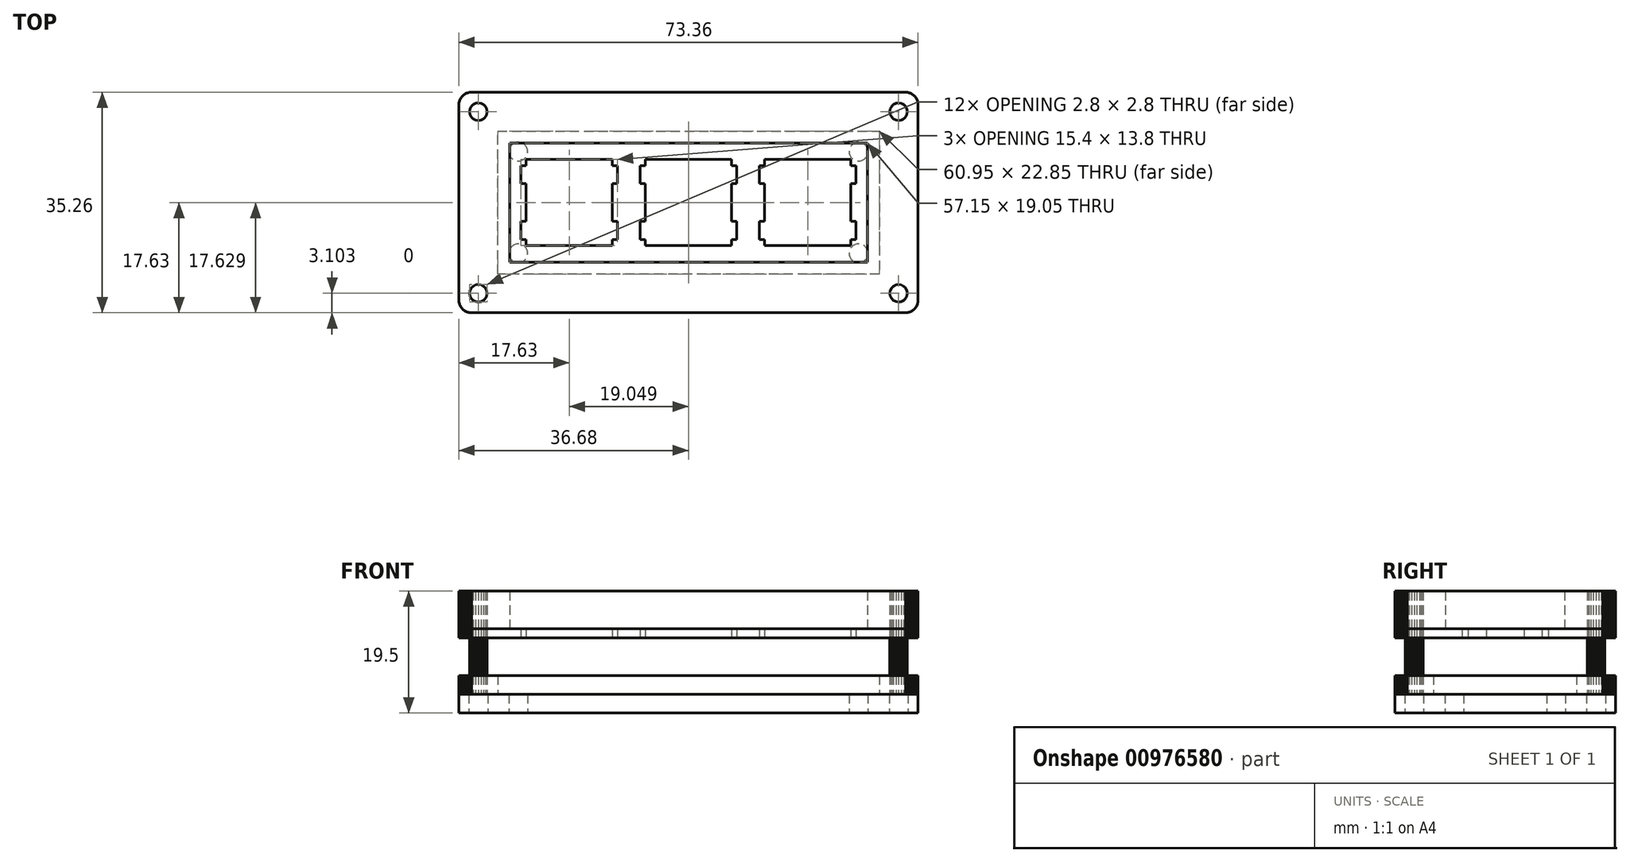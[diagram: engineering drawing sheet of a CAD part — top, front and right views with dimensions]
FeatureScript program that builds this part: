
annotation { "Feature Type Name" : "Feature", "Feature Type Description" : "" }
export const myFeature = defineFeature(function(context is Context, id is Id, definition is map)
    precondition{}
    {
        {
            assignVariable(context, id + "F0", {"name" : "Thickness", "anyValue" : 3});
        }
        {
            var Q0;
            Q0=qCreatedBy(makeId("Top.planeOp"),FACE);
            var sketch = newSketch(context, id + "F1", { "sketchPlane" : qUnion([Q0])});
            skLineSegment(sketch, "E0", {"start": v(36.68, 15.63) * mm, "end": v(36.68, -15.63) * mm});
            skLineSegment(sketch, "E1", {"start": v(34.68, -17.63) * mm, "end": v(-34.68, -17.63) * mm});
            skLineSegment(sketch, "E2", {"start": v(-36.68, -15.63) * mm, "end": v(-36.68, 15.63) * mm});
            skLineSegment(sketch, "E3", {"start": v(-34.68, 17.63) * mm, "end": v(34.68, 17.63) * mm});
            skCircle(sketch, "E4", {"center": v(-27.18, 8.13) * mm, "radius": 1.5 * mm});
            skCircle(sketch, "E5", {"center": v(-27.18, 8.13) * mm, "radius": 9.5 * mm, "construction": true});
            skPoint(sketch, "E6.visualSharp", {"position": v(-36.68, -17.63) * mm});
            skArc(sketch, "E6.filletArc", {"start": v(-36.68, -15.63) * mm, "mid": v(-36.09, -17.04) * mm, "end": v(-34.68, -17.63) * mm});
            skPoint(sketch, "E7.visualSharp", {"position": v(36.68, -17.63) * mm});
            skArc(sketch, "E7.filletArc", {"start": v(34.68, -17.63) * mm, "mid": v(36.09, -17.04) * mm, "end": v(36.68, -15.63) * mm});
            skPoint(sketch, "E8.visualSharp", {"position": v(36.68, 17.63) * mm});
            skArc(sketch, "E8.filletArc", {"start": v(36.68, 15.63) * mm, "mid": v(36.09, 17.04) * mm, "end": v(34.68, 17.63) * mm});
            skPoint(sketch, "E9.visualSharp", {"position": v(-36.68, 17.63) * mm});
            skArc(sketch, "E9.filletArc", {"start": v(-34.68, 17.63) * mm, "mid": v(-36.09, 17.04) * mm, "end": v(-36.68, 15.63) * mm});
            skCircle(sketch, "E10", {"center": v(33.58, 14.53) * mm, "radius": 3.1 * mm, "construction": true});
            skCircle(sketch, "E11", {"center": v(33.58, 14.53) * mm, "radius": 1.5 * mm});
            skCircle(sketch, "E12.MirrorC", {"center": v(33.58, -14.53) * mm, "radius": 1.5 * mm});
            skCircle(sketch, "E13.MirrorC", {"center": v(-33.58, 14.53) * mm, "radius": 1.5 * mm});
            skCircle(sketch, "E14.MirrorC", {"center": v(-33.58, -14.53) * mm, "radius": 1.5 * mm});
            skCircle(sketch, "E15.MirrorC", {"center": v(27.18, 8.13) * mm, "radius": 1.5 * mm});
            skCircle(sketch, "E16.MirrorC", {"center": v(-27.18, -8.13) * mm, "radius": 1.5 * mm});
            skCircle(sketch, "E17.MirrorC", {"center": v(27.18, -8.13) * mm, "radius": 1.5 * mm});
            skSolve(sketch);
        }
        {
            var Q0;
            Q0 = qSketchRegion(id + "F1", true);
            extrude(context, id + "F2", {"entities" : qUnion([Q0]), "depth" : (getVariable(context, 'Thickness')) * mm, "offsetDistance" : 25 * mm});
        }
        {
            var Q0;
            Q0=makeQuery(id+"F2.opExtrude","CAP_FACE",FACE,{"disambiguationData":[OSD([sQuery(id+"F1.wireOp",EDGE,"f38d5113-8ffd-432d-a3ce-a915938ce8ef"),sQuery(id+"F1.wireOp",EDGE,"30d00d2a-8399-40ac-ba43-e3ae4fa62f4f"),sQuery(id+"F1.wireOp",EDGE,"33de4b6a-8df2-4582-920f-f16a76d6a48d"),sQuery(id+"F1.wireOp",EDGE,"dd7a822c-130c-4706-b44d-d1e14abfd110"),sQuery(id+"F1.wireOp",EDGE,"c533de15-2e03-4a6f-b7a6-2e9cb061479b"),sQuery(id+"F1.wireOp",EDGE,"1dfa1c6c-949b-4392-be26-7293bec304e9"),sQuery(id+"F1.wireOp",EDGE,"79b63b09-4684-42a3-82d4-33271dc96dd7"),sQuery(id+"F1.wireOp",EDGE,"c6cd64e9-58d5-430f-8fd8-64eae907adb3"),sQuery(id+"F1.wireOp",EDGE,"a9528a18-83ce-47e4-8030-754601af9eb3"),sQuery(id+"F1.wireOp",EDGE,"cd46a195-92e7-4e63-b4f0-881a531f52bb"),sQuery(id+"F1.wireOp",EDGE,"56d33d33-9960-4a7a-86af-0e57c873a139"),sQuery(id+"F1.wireOp",EDGE,"8febe79d-c26d-47ca-a997-6ddbf6247f7f"),sQuery(id+"F1.wireOp",EDGE,"1b81442f-1442-4f9c-ac81-b0700e3801b3"),sQuery(id+"F1.wireOp",EDGE,"bce25026-a245-4289-a49b-b4b12a412b04"),sQuery(id+"F1.wireOp",EDGE,"256a1b4b-6397-493c-808c-40f05bf4c5e3"),sQuery(id+"F1.wireOp",EDGE,"982427ee-fb93-4e7f-9e5f-c007e6e26276"),sQuery(id+"F1.wireOp",EDGE,"e8128256-5901-4357-a0be-eaef1402cac8"),sQuery(id+"F1.wireOp",EDGE,"ce55bd8c-7602-4f65-abef-ba81b887f1be"),sQuery(id+"F1.wireOp",EDGE,"389a8022-4a1a-4ebd-a71b-27301e9d4ff6"),sQuery(id+"F1.wireOp",EDGE,"ce64c4c0-22d1-436f-a547-7537afd4866e"),sQuery(id+"F1.wireOp",EDGE,"E0"),sQuery(id+"F1.wireOp",EDGE,"e7bae28c-2ccc-4f20-96f0-a530882d5159"),sQuery(id+"F1.wireOp",EDGE,"1336ac6d-c182-419d-8f47-5aac0d18e762"),sQuery(id+"F1.wireOp",EDGE,"b2a7ba0f-895a-4bb6-a783-6d883c045cbe"),sQuery(id+"F1.wireOp",EDGE,"51b79f1e-a1b5-4bf4-937f-2afb163cf299"),sQuery(id+"F1.wireOp",EDGE,"549b87ac-e324-453b-b570-1453983d1911"),sQuery(id+"F1.wireOp",EDGE,"4242826b-0d45-4b2e-b694-fd388aa842fb"),sQuery(id+"F1.wireOp",EDGE,"c10ba44a-b5aa-45ae-bf6a-75690cab2dd6"),sQuery(id+"F1.wireOp",EDGE,"8177ea96-e12c-463d-a123-4af6399735c3"),sQuery(id+"F1.wireOp",EDGE,"58842294-a54e-47b9-86a7-91804475791d"),sQuery(id+"F1.wireOp",EDGE,"1daaa4ac-2799-49ed-8cf0-012224148010"),sQuery(id+"F1.wireOp",EDGE,"a375905a-4df6-48c9-a9bc-60ca1bae9196"),sQuery(id+"F1.wireOp",EDGE,"df5412a8-c126-4beb-a6d7-e5caac17dc0e"),sQuery(id+"F1.wireOp",EDGE,"0a7991f6-c764-42fb-b197-93e5d7973440"),sQuery(id+"F1.wireOp",EDGE,"db6fbf27-b7a6-43e2-ad22-b1f5cb7f6f55"),sQuery(id+"F1.wireOp",EDGE,"c78e91c3-a6b3-40c6-9ba2-7427c3ae4570"),sQuery(id+"F1.wireOp",EDGE,"1da2b595-4f5a-4a08-b72b-7e329805d670"),sQuery(id+"F1.wireOp",EDGE,"b998bcce-a593-4696-85a6-c582ec4e01af"),sQuery(id+"F1.wireOp",EDGE,"3c900711-9d2c-45f7-b880-0ee555895d99"),sQuery(id+"F1.wireOp",EDGE,"a664491b-32bc-47fb-82bc-0ab575ecea55"),sQuery(id+"F1.wireOp",EDGE,"0b5283cb-b386-4d68-bacd-65cfa7a1c687"),sQuery(id+"F1.wireOp",EDGE,"E1"),sQuery(id+"F1.wireOp",EDGE,"dc151aaf-655b-4e22-9e08-b51a414cdedc"),sQuery(id+"F1.wireOp",EDGE,"49712529-a297-4864-9951-9f888228fd79"),sQuery(id+"F1.wireOp",EDGE,"e018c4f9-948b-427d-ab6c-159fd14e4654"),sQuery(id+"F1.wireOp",EDGE,"b4c8d362-4280-49e8-b707-11ba0145ad9e"),sQuery(id+"F1.wireOp",EDGE,"e4ff2872-b3dd-4565-8f3a-b1d815be933f"),sQuery(id+"F1.wireOp",EDGE,"4f95d7c4-3227-4e30-a015-5dc2aef1d5b8"),sQuery(id+"F1.wireOp",EDGE,"7d5e0655-794f-4f1c-811a-7c8bca8cb441"),sQuery(id+"F1.wireOp",EDGE,"06cd70f3-8a57-4482-8df6-4ae0e3f2c176"),sQuery(id+"F1.wireOp",EDGE,"79ffc42a-8afc-40c3-b99c-81495eff8d88"),sQuery(id+"F1.wireOp",EDGE,"42f66c54-dfdb-4538-af7b-f42205d213f2"),sQuery(id+"F1.wireOp",EDGE,"4107d0d6-0b50-4649-80d2-5ef7e23b521e"),sQuery(id+"F1.wireOp",EDGE,"40e89e02-920e-4762-a084-e2b73f78281e"),sQuery(id+"F1.wireOp",EDGE,"fe9b1155-c610-44b2-a0b0-31eb3f0e455a"),sQuery(id+"F1.wireOp",EDGE,"73f3c45d-f342-4798-9e75-ac507e4c3c51"),sQuery(id+"F1.wireOp",EDGE,"094ff1a6-3b8b-4ac9-81fa-9bd9003943b7"),sQuery(id+"F1.wireOp",EDGE,"f8d24ccc-6bb8-41f9-afa7-affc31c8a13a"),sQuery(id+"F1.wireOp",EDGE,"f2db9464-d5ad-4da8-bc6d-19101f4076d9"),sQuery(id+"F1.wireOp",EDGE,"defc6b11-d794-425b-b4a3-06b1fb4b3a05"),sQuery(id+"F1.wireOp",EDGE,"abc8f65d-411d-4283-8a50-7cb67d340370"),sQuery(id+"F1.wireOp",EDGE,"cac6a9b9-9d93-4d5c-ad04-d05eb65cdc37"),sQuery(id+"F1.wireOp",EDGE,"E2"),sQuery(id+"F1.wireOp",EDGE,"1b493a45-cd4b-48a1-8403-62bc6a5772fd"),sQuery(id+"F1.wireOp",EDGE,"3576eeaf-6626-4881-aa94-039e0b64bb02"),sQuery(id+"F1.wireOp",EDGE,"5d0b7610-6fbf-4a3c-89f8-b3cf9798b51e"),sQuery(id+"F1.wireOp",EDGE,"ef7b6dab-872b-43b9-8f18-2a554d21f1c5"),sQuery(id+"F1.wireOp",EDGE,"702b8a5a-b0f8-4392-bb79-e2564fd4a175"),sQuery(id+"F1.wireOp",EDGE,"fb67655c-e3e3-4c0d-af6e-f14e7b25c453"),sQuery(id+"F1.wireOp",EDGE,"84ab0164-69e0-4c3c-a998-7971c5eca7ff"),sQuery(id+"F1.wireOp",EDGE,"f57c4b1b-64ee-44b1-9523-b8aed98779c7"),sQuery(id+"F1.wireOp",EDGE,"c5eadbd6-3ef8-4954-b175-27f3b5fe7724"),sQuery(id+"F1.wireOp",EDGE,"9ed46d83-222e-4792-a6c7-6fce6fe02704"),sQuery(id+"F1.wireOp",EDGE,"89c49cfb-4cd2-4b6f-8936-88e12b2d1e60"),sQuery(id+"F1.wireOp",EDGE,"4376ecf0-2db7-4b48-bea3-0de71fc5ea1c"),sQuery(id+"F1.wireOp",EDGE,"75b1cf93-37d0-4452-91ae-a9c5d2c97683"),sQuery(id+"F1.wireOp",EDGE,"3614327f-aa34-4ffd-8e4f-bcaeb5bf0a6c"),sQuery(id+"F1.wireOp",EDGE,"779057a4-3d89-47b9-81ca-a53b9e90171e"),sQuery(id+"F1.wireOp",EDGE,"6ee2b408-d537-4a72-87c2-fd9683a19ca6"),sQuery(id+"F1.wireOp",EDGE,"23edfa7d-6738-4f5a-81be-73427f6a28ee"),sQuery(id+"F1.wireOp",EDGE,"e48bd3fa-4649-480f-9b1a-c6254d94e219"),sQuery(id+"F1.wireOp",EDGE,"12005d63-deb8-4797-ae3c-77c9ec96a49e"),sQuery(id+"F1.wireOp",EDGE,"5feb5ef9-fb39-4188-8368-4f7ee21595f9"),sQuery(id+"F1.wireOp",EDGE,"E3"),sQuery(id+"F1.wireOp",EDGE,"375d05a5-7352-4c2e-8e15-ec4b736729b3"),sQuery(id+"F1.wireOp",EDGE,"9c3f83da-1f49-4fda-8ace-305589c114e8"),sQuery(id+"F1.wireOp",EDGE,"e43f68f6-8ff6-4711-b354-2877b85f6b52"),sQuery(id+"F1.wireOp",EDGE,"394ec990-2034-4773-98bf-db41d7d77632"),sQuery(id+"F1.wireOp",EDGE,"46e4831f-40e9-440f-8ed1-3a2241c78b93"),sQuery(id+"F1.wireOp",EDGE,"f4095387-cf87-4e47-8a17-b0a48ba5ff53"),sQuery(id+"F1.wireOp",EDGE,"3431f221-8c6b-4c8f-bf39-b26068e9f50f"),sQuery(id+"F1.wireOp",EDGE,"bb056c9b-5b6d-4ca5-8551-39ef673d3e90"),sQuery(id+"F1.wireOp",EDGE,"e86cdd79-84d4-4ae2-97f3-4e6ae3081eea"),sQuery(id+"F1.wireOp",EDGE,"c809a6d1-a85f-4b8a-837b-231e69f3aaeb"),sQuery(id+"F1.wireOp",EDGE,"07d301be-e16b-42f0-830b-e997eeee4490"),sQuery(id+"F1.wireOp",EDGE,"55ebaf8e-f23b-4a48-8e95-bc4ef2f236b7"),sQuery(id+"F1.wireOp",EDGE,"378850fb-ba34-45b4-8740-714a5133ff22"),sQuery(id+"F1.wireOp",EDGE,"3ae367b7-d643-4276-85e9-6a23ddf29430"),sQuery(id+"F1.wireOp",EDGE,"53d4f895-4ed9-488b-b0d1-f3c2c6c759e0"),sQuery(id+"F1.wireOp",EDGE,"f76b93d0-b9fe-42bd-b2e6-eec567e21316"),sQuery(id+"F1.wireOp",EDGE,"a639c885-3a3c-43bd-b63e-b20f27626dc6"),sQuery(id+"F1.wireOp",EDGE,"0956502c-505e-4620-a3f0-5d52484e5646"),sQuery(id+"F1.wireOp",EDGE,"7bebd568-8fb5-461b-a5fa-e6a58b129612"),sQuery(id+"F1.wireOp",EDGE,"a6843f68-7bac-4147-bc07-735a5e6c75ad"),sQuery(id+"F1.wireOp",EDGE,"e7422b1a-2ff4-47a3-bda7-08b2a937d9f9"),sQuery(id+"F1.wireOp",EDGE,"65a62e1f-1bdc-415a-8738-9de6c800868c"),sQuery(id+"F1.wireOp",EDGE,"f343366e-88c6-4ccb-b5ad-f437e8845c66"),sQuery(id+"F1.wireOp",EDGE,"277da469-a2c5-48fb-bffd-6a987a576b23"),sQuery(id+"F1.wireOp",EDGE,"78d797f1-53d3-4fe6-8882-1b8bdd95c457"),sQuery(id+"F1.wireOp",EDGE,"df65fc30-7cc9-4eed-8bc0-fe88d6a05837"),sQuery(id+"F1.wireOp",EDGE,"b249785e-f4de-444a-9550-27b038c79378"),sQuery(id+"F1.wireOp",EDGE,"a321804d-ac7d-4f63-8178-42e58f7c23b8"),sQuery(id+"F1.wireOp",EDGE,"e865e5c9-37cc-44bd-ad3e-1d2792b206ed"),sQuery(id+"F1.wireOp",EDGE,"aed35ace-35c3-4fdb-94dc-0c1b6703f088"),sQuery(id+"F1.wireOp",EDGE,"afe1609f-2fea-4249-8daf-8fa0940d6594"),sQuery(id+"F1.wireOp",EDGE,"0e007c15-1edc-460a-950a-628008027a47"),sQuery(id+"F1.wireOp",EDGE,"877074a5-9ac3-48fa-867a-f39cee54b54e"),sQuery(id+"F1.wireOp",EDGE,"4be27524-87f7-4113-ab5b-64a9e3fb53f4"),sQuery(id+"F1.wireOp",EDGE,"821f041e-bc04-4d1c-8ca6-d2a133688fe3"),sQuery(id+"F1.wireOp",EDGE,"e8f4a7f0-f644-491e-a36b-0aac7bdaf42b"),sQuery(id+"F1.wireOp",EDGE,"2e308115-14ea-46d2-b3cd-cfaca5673bca"),sQuery(id+"F1.wireOp",EDGE,"453a263e-b029-469e-853b-c8e9e39a1490"),sQuery(id+"F1.wireOp",EDGE,"204495ba-ad6b-447d-95d0-1329485139ee"),sQuery(id+"F1.wireOp",EDGE,"76f8445f-3039-40e3-b59d-1c2e07baca66"),sQuery(id+"F1.wireOp",EDGE,"c2ae28a4-42c7-4c6c-9a46-b00a058cec62"),sQuery(id+"F1.wireOp",EDGE,"4a4df088-07fa-4c99-a81b-767c68b6d1d8"),sQuery(id+"F1.wireOp",EDGE,"aae6b3e1-77b0-412b-8c80-e1abb44d3504"),sQuery(id+"F1.wireOp",EDGE,"f405fb20-aac6-4ca1-9ce9-75b51006ae97"),sQuery(id+"F1.wireOp",EDGE,"4fb9fad2-deea-42f1-829c-a2a4f4298183"),sQuery(id+"F1.wireOp",EDGE,"a7850f09-c898-4094-9555-75542e55ded4"),sQuery(id+"F1.wireOp",EDGE,"aa5d9858-176d-4154-9ff8-5faaefc81662"),sQuery(id+"F1.wireOp",EDGE,"2d9059a2-4419-484d-9736-3055773689bc"),sQuery(id+"F1.wireOp",EDGE,"dd3dcc80-84e9-489b-bb2f-4473fcd80f19"),sQuery(id+"F1.wireOp",EDGE,"dcbebcdd-d753-421a-b7fa-6c7ee5e31440"),sQuery(id+"F1.wireOp",EDGE,"503f3d43-6d1f-4ee7-b547-a8fd725fb3ab"),sQuery(id+"F1.wireOp",EDGE,"cd25b7c8-12c3-4c02-9a23-7ef7c307f70c"),sQuery(id+"F1.wireOp",EDGE,"119eede6-abee-4cc1-aace-7f85755239c6"),sQuery(id+"F1.wireOp",EDGE,"35b08199-87a7-4231-9ef0-b648b0b0a317"),sQuery(id+"F1.wireOp",EDGE,"ef969a36-0c32-43bc-a5cc-de44b6f653fd"),sQuery(id+"F1.wireOp",EDGE,"d7d3e627-047a-43d1-8c58-7a8ba0f68a38"),sQuery(id+"F1.wireOp",EDGE,"a37be8a1-0f78-4a13-b5c7-35c9caa28138"),sQuery(id+"F1.wireOp",EDGE,"25e40d26-ae31-4d37-9d84-6be22b0346fb"),sQuery(id+"F1.wireOp",EDGE,"0ad05f7a-b801-445c-b4f5-407a055fee7d"),sQuery(id+"F1.wireOp",EDGE,"e18f7e26-7bfc-428b-b7c8-318b3738c7ce"),sQuery(id+"F1.wireOp",EDGE,"3caf87b9-ecdf-4159-8513-dbcb366781fe"),sQuery(id+"F1.wireOp",EDGE,"0adb193c-d4bd-405b-bcc1-885a563c7004"),sQuery(id+"F1.wireOp",EDGE,"cc23c10c-569a-4268-991d-ab9510c1ae04"),sQuery(id+"F1.wireOp",EDGE,"3bc30580-8930-4d54-80e0-1c6bc3bb6887"),sQuery(id+"F1.wireOp",EDGE,"79df71d2-95d8-4c47-8dac-8bb4a9cef6f8"),sQuery(id+"F1.wireOp",EDGE,"ea5ffc43-eeaa-4756-9892-e087e510553f"),sQuery(id+"F1.wireOp",EDGE,"43901534-6a02-4f5e-90d8-08fae777d5cc"),sQuery(id+"F1.wireOp",EDGE,"c616b6b5-51f4-4ef5-b0f0-351437958c84"),sQuery(id+"F1.wireOp",EDGE,"02a18fd8-67f2-458f-912a-2a7f7385ceb3"),sQuery(id+"F1.wireOp",EDGE,"b3a5ed1d-463b-489b-bab5-6900b963e241"),sQuery(id+"F1.wireOp",EDGE,"b7ecbeb7-b34d-49d8-84c1-67e130cbed5f"),sQuery(id+"F1.wireOp",EDGE,"d1f06dae-498a-4cff-aebc-f13ce39c8cfa"),sQuery(id+"F1.wireOp",EDGE,"89000d0c-59a2-4536-893b-37c8f4f88398"),sQuery(id+"F1.wireOp",EDGE,"ca62e9c7-3f18-458a-a2eb-147d3a984930"),sQuery(id+"F1.wireOp",EDGE,"63a744c9-809e-44df-bd20-1c76d192e900"),sQuery(id+"F1.wireOp",EDGE,"08ed6b55-01fe-48f6-a80c-625b2d74a1d8"),sQuery(id+"F1.wireOp",EDGE,"17c2d004-1ab6-45b4-8d3f-5b340bac2396"),sQuery(id+"F1.wireOp",EDGE,"451c9bbb-4c33-4b3d-9fd2-577128ce0c50"),sQuery(id+"F1.wireOp",EDGE,"b970bcd2-71ad-4ecd-bbdc-8d159682d01d"),sQuery(id+"F1.wireOp",EDGE,"ca72fe7f-d493-4aee-9c30-cad0c3f508d1")])],"isStart":false});
            var sketch = newSketch(context, id + "F3", { "sketchPlane" : qUnion([Q0])});
            skLineSegment(sketch, "E18", {"start": v(34.68, 17.62) * mm, "end": v(34.83, 17.62) * mm});
            skLineSegment(sketch, "E19", {"start": v(34.83, 17.62) * mm, "end": v(34.99, 17.6) * mm});
            skLineSegment(sketch, "E20", {"start": v(34.99, 17.6) * mm, "end": v(35.14, 17.57) * mm});
            skLineSegment(sketch, "E21", {"start": v(35.14, 17.57) * mm, "end": v(35.3, 17.53) * mm});
            skLineSegment(sketch, "E22", {"start": v(35.3, 17.53) * mm, "end": v(35.44, 17.47) * mm});
            skLineSegment(sketch, "E23", {"start": v(35.44, 17.47) * mm, "end": v(35.58, 17.4) * mm});
            skLineSegment(sketch, "E24", {"start": v(35.58, 17.4) * mm, "end": v(35.72, 17.33) * mm});
            skLineSegment(sketch, "E25", {"start": v(35.72, 17.33) * mm, "end": v(35.85, 17.24) * mm});
            skLineSegment(sketch, "E26", {"start": v(35.85, 17.24) * mm, "end": v(35.97, 17.15) * mm});
            skLineSegment(sketch, "E27", {"start": v(35.97, 17.15) * mm, "end": v(36.1, 17.04) * mm});
            skLineSegment(sketch, "E28", {"start": v(36.1, 17.04) * mm, "end": v(36.2, 16.92) * mm});
            skLineSegment(sketch, "E29", {"start": v(36.2, 16.92) * mm, "end": v(36.3, 16.8) * mm});
            skLineSegment(sketch, "E30", {"start": v(36.3, 16.8) * mm, "end": v(36.38, 16.67) * mm});
            skLineSegment(sketch, "E31", {"start": v(36.38, 16.67) * mm, "end": v(36.46, 16.53) * mm});
            skLineSegment(sketch, "E32", {"start": v(36.46, 16.53) * mm, "end": v(36.52, 16.4) * mm});
            skLineSegment(sketch, "E33", {"start": v(36.52, 16.4) * mm, "end": v(36.58, 16.24) * mm});
            skLineSegment(sketch, "E34", {"start": v(36.58, 16.24) * mm, "end": v(36.62, 16.1) * mm});
            skLineSegment(sketch, "E35", {"start": v(36.62, 16.1) * mm, "end": v(36.65, 15.94) * mm});
            skLineSegment(sketch, "E36", {"start": v(36.65, 15.94) * mm, "end": v(36.67, 15.78) * mm});
            skLineSegment(sketch, "E37", {"start": v(36.67, 15.78) * mm, "end": v(36.68, 15.62) * mm});
            skLineSegment(sketch, "E38", {"start": v(36.68, 15.62) * mm, "end": v(36.68, -15.63) * mm});
            skLineSegment(sketch, "E39", {"start": v(36.68, -15.63) * mm, "end": v(36.67, -15.78) * mm});
            skLineSegment(sketch, "E40", {"start": v(36.67, -15.78) * mm, "end": v(36.65, -15.94) * mm});
            skLineSegment(sketch, "E41", {"start": v(36.65, -15.94) * mm, "end": v(36.62, -16.1) * mm});
            skLineSegment(sketch, "E42", {"start": v(36.62, -16.1) * mm, "end": v(36.58, -16.24) * mm});
            skLineSegment(sketch, "E43", {"start": v(36.58, -16.24) * mm, "end": v(36.52, -16.4) * mm});
            skLineSegment(sketch, "E44", {"start": v(36.52, -16.4) * mm, "end": v(36.46, -16.53) * mm});
            skLineSegment(sketch, "E45", {"start": v(36.46, -16.53) * mm, "end": v(36.38, -16.67) * mm});
            skLineSegment(sketch, "E46", {"start": v(36.38, -16.67) * mm, "end": v(36.3, -16.8) * mm});
            skLineSegment(sketch, "E47", {"start": v(36.3, -16.8) * mm, "end": v(36.2, -16.92) * mm});
            skLineSegment(sketch, "E48", {"start": v(36.2, -16.92) * mm, "end": v(36.1, -17.04) * mm});
            skLineSegment(sketch, "E49", {"start": v(36.1, -17.04) * mm, "end": v(35.97, -17.15) * mm});
            skLineSegment(sketch, "E50", {"start": v(35.97, -17.15) * mm, "end": v(35.85, -17.24) * mm});
            skLineSegment(sketch, "E51", {"start": v(35.85, -17.24) * mm, "end": v(35.72, -17.33) * mm});
            skLineSegment(sketch, "E52", {"start": v(35.72, -17.33) * mm, "end": v(35.58, -17.4) * mm});
            skLineSegment(sketch, "E53", {"start": v(35.58, -17.4) * mm, "end": v(35.44, -17.47) * mm});
            skLineSegment(sketch, "E54", {"start": v(35.44, -17.47) * mm, "end": v(35.3, -17.53) * mm});
            skLineSegment(sketch, "E55", {"start": v(35.3, -17.53) * mm, "end": v(35.14, -17.57) * mm});
            skLineSegment(sketch, "E56", {"start": v(35.14, -17.57) * mm, "end": v(34.99, -17.6) * mm});
            skLineSegment(sketch, "E57", {"start": v(34.99, -17.6) * mm, "end": v(34.83, -17.62) * mm});
            skLineSegment(sketch, "E58", {"start": v(34.83, -17.62) * mm, "end": v(34.68, -17.63) * mm});
            skLineSegment(sketch, "E59", {"start": v(34.68, -17.63) * mm, "end": v(-34.67, -17.63) * mm});
            skLineSegment(sketch, "E60", {"start": v(-34.67, -17.63) * mm, "end": v(-34.83, -17.62) * mm});
            skLineSegment(sketch, "E61", {"start": v(-34.83, -17.62) * mm, "end": v(-34.99, -17.6) * mm});
            skLineSegment(sketch, "E62", {"start": v(-34.99, -17.6) * mm, "end": v(-35.14, -17.57) * mm});
            skLineSegment(sketch, "E63", {"start": v(-35.14, -17.57) * mm, "end": v(-35.3, -17.53) * mm});
            skLineSegment(sketch, "E64", {"start": v(-35.3, -17.53) * mm, "end": v(-35.44, -17.47) * mm});
            skLineSegment(sketch, "E65", {"start": v(-35.44, -17.47) * mm, "end": v(-35.58, -17.4) * mm});
            skLineSegment(sketch, "E66", {"start": v(-35.58, -17.4) * mm, "end": v(-35.72, -17.33) * mm});
            skLineSegment(sketch, "E67", {"start": v(-35.72, -17.33) * mm, "end": v(-35.85, -17.24) * mm});
            skLineSegment(sketch, "E68", {"start": v(-35.85, -17.24) * mm, "end": v(-35.97, -17.15) * mm});
            skLineSegment(sketch, "E69", {"start": v(-35.97, -17.15) * mm, "end": v(-36.1, -17.04) * mm});
            skLineSegment(sketch, "E70", {"start": v(-36.1, -17.04) * mm, "end": v(-36.2, -16.92) * mm});
            skLineSegment(sketch, "E71", {"start": v(-36.2, -16.92) * mm, "end": v(-36.3, -16.8) * mm});
            skLineSegment(sketch, "E72", {"start": v(-36.3, -16.8) * mm, "end": v(-36.38, -16.67) * mm});
            skLineSegment(sketch, "E73", {"start": v(-36.38, -16.67) * mm, "end": v(-36.46, -16.53) * mm});
            skLineSegment(sketch, "E74", {"start": v(-36.46, -16.53) * mm, "end": v(-36.52, -16.4) * mm});
            skLineSegment(sketch, "E75", {"start": v(-36.52, -16.4) * mm, "end": v(-36.58, -16.24) * mm});
            skLineSegment(sketch, "E76", {"start": v(-36.58, -16.24) * mm, "end": v(-36.62, -16.1) * mm});
            skLineSegment(sketch, "E77", {"start": v(-36.62, -16.1) * mm, "end": v(-36.65, -15.94) * mm});
            skLineSegment(sketch, "E78", {"start": v(-36.65, -15.94) * mm, "end": v(-36.67, -15.78) * mm});
            skLineSegment(sketch, "E79", {"start": v(-36.67, -15.78) * mm, "end": v(-36.68, -15.62) * mm});
            skLineSegment(sketch, "E80", {"start": v(-36.68, -15.62) * mm, "end": v(-36.67, 15.62) * mm});
            skLineSegment(sketch, "E81", {"start": v(-36.67, 15.62) * mm, "end": v(-36.67, 15.78) * mm});
            skLineSegment(sketch, "E82", {"start": v(-36.67, 15.78) * mm, "end": v(-36.65, 15.94) * mm});
            skLineSegment(sketch, "E83", {"start": v(-36.65, 15.94) * mm, "end": v(-36.62, 16.1) * mm});
            skLineSegment(sketch, "E84", {"start": v(-36.62, 16.1) * mm, "end": v(-36.58, 16.24) * mm});
            skLineSegment(sketch, "E85", {"start": v(-36.58, 16.24) * mm, "end": v(-36.52, 16.4) * mm});
            skLineSegment(sketch, "E86", {"start": v(-36.52, 16.4) * mm, "end": v(-36.46, 16.53) * mm});
            skLineSegment(sketch, "E87", {"start": v(-36.46, 16.53) * mm, "end": v(-36.38, 16.67) * mm});
            skLineSegment(sketch, "E88", {"start": v(-36.38, 16.67) * mm, "end": v(-36.3, 16.8) * mm});
            skLineSegment(sketch, "E89", {"start": v(-36.3, 16.8) * mm, "end": v(-36.2, 16.92) * mm});
            skLineSegment(sketch, "E90", {"start": v(-36.2, 16.92) * mm, "end": v(-36.1, 17.04) * mm});
            skLineSegment(sketch, "E91", {"start": v(-36.1, 17.04) * mm, "end": v(-35.97, 17.15) * mm});
            skLineSegment(sketch, "E92", {"start": v(-35.97, 17.15) * mm, "end": v(-35.85, 17.24) * mm});
            skLineSegment(sketch, "E93", {"start": v(-35.85, 17.24) * mm, "end": v(-35.72, 17.33) * mm});
            skLineSegment(sketch, "E94", {"start": v(-35.72, 17.33) * mm, "end": v(-35.58, 17.4) * mm});
            skLineSegment(sketch, "E95", {"start": v(-35.58, 17.4) * mm, "end": v(-35.44, 17.47) * mm});
            skLineSegment(sketch, "E96", {"start": v(-35.44, 17.47) * mm, "end": v(-35.3, 17.53) * mm});
            skLineSegment(sketch, "E97", {"start": v(-35.3, 17.53) * mm, "end": v(-35.14, 17.57) * mm});
            skLineSegment(sketch, "E98", {"start": v(-35.14, 17.57) * mm, "end": v(-34.99, 17.6) * mm});
            skLineSegment(sketch, "E99", {"start": v(-34.99, 17.6) * mm, "end": v(-34.83, 17.62) * mm});
            skLineSegment(sketch, "E100", {"start": v(-34.83, 17.62) * mm, "end": v(-34.67, 17.63) * mm});
            skLineSegment(sketch, "E101", {"start": v(-34.67, 17.63) * mm, "end": v(34.68, 17.62) * mm});
            skLineSegment(sketch, "E102", {"start": v(33.14, -13.2) * mm, "end": v(32.75, -13.4) * mm});
            skLineSegment(sketch, "E103", {"start": v(32.75, -13.4) * mm, "end": v(32.44, -13.7) * mm});
            skLineSegment(sketch, "E104", {"start": v(32.44, -13.7) * mm, "end": v(32.24, -14.1) * mm});
            skLineSegment(sketch, "E105", {"start": v(32.24, -14.1) * mm, "end": v(32.18, -14.53) * mm});
            skLineSegment(sketch, "E106", {"start": v(32.18, -14.53) * mm, "end": v(32.24, -14.96) * mm});
            skLineSegment(sketch, "E107", {"start": v(32.24, -14.96) * mm, "end": v(32.44, -15.35) * mm});
            skLineSegment(sketch, "E108", {"start": v(32.44, -15.35) * mm, "end": v(32.75, -15.66) * mm});
            skLineSegment(sketch, "E109", {"start": v(32.75, -15.66) * mm, "end": v(33.14, -15.86) * mm});
            skLineSegment(sketch, "E110", {"start": v(33.14, -15.86) * mm, "end": v(33.58, -15.93) * mm});
            skLineSegment(sketch, "E111", {"start": v(33.58, -15.93) * mm, "end": v(34, -15.86) * mm});
            skLineSegment(sketch, "E112", {"start": v(34, -15.86) * mm, "end": v(34.4, -15.66) * mm});
            skLineSegment(sketch, "E113", {"start": v(34.4, -15.66) * mm, "end": v(34.7, -15.35) * mm});
            skLineSegment(sketch, "E114", {"start": v(34.7, -15.35) * mm, "end": v(34.9, -14.96) * mm});
            skLineSegment(sketch, "E115", {"start": v(34.9, -14.96) * mm, "end": v(34.98, -14.53) * mm});
            skLineSegment(sketch, "E116", {"start": v(34.98, -14.53) * mm, "end": v(34.9, -14.1) * mm});
            skLineSegment(sketch, "E117", {"start": v(34.9, -14.1) * mm, "end": v(34.7, -13.7) * mm});
            skLineSegment(sketch, "E118", {"start": v(34.7, -13.7) * mm, "end": v(34.4, -13.4) * mm});
            skLineSegment(sketch, "E119", {"start": v(34.4, -13.4) * mm, "end": v(34, -13.2) * mm});
            skLineSegment(sketch, "E120", {"start": v(34, -13.2) * mm, "end": v(33.58, -13.13) * mm});
            skLineSegment(sketch, "E121", {"start": v(33.58, -13.13) * mm, "end": v(33.14, -13.2) * mm});
            skLineSegment(sketch, "E122", {"start": v(-34, -13.2) * mm, "end": v(-34.4, -13.4) * mm});
            skLineSegment(sketch, "E123", {"start": v(-34.4, -13.4) * mm, "end": v(-34.7, -13.7) * mm});
            skLineSegment(sketch, "E124", {"start": v(-34.7, -13.7) * mm, "end": v(-34.9, -14.1) * mm});
            skLineSegment(sketch, "E125", {"start": v(-34.9, -14.1) * mm, "end": v(-34.98, -14.53) * mm});
            skLineSegment(sketch, "E126", {"start": v(-34.98, -14.53) * mm, "end": v(-34.9, -14.96) * mm});
            skLineSegment(sketch, "E127", {"start": v(-34.9, -14.96) * mm, "end": v(-34.7, -15.35) * mm});
            skLineSegment(sketch, "E128", {"start": v(-34.7, -15.35) * mm, "end": v(-34.4, -15.66) * mm});
            skLineSegment(sketch, "E129", {"start": v(-34.4, -15.66) * mm, "end": v(-34, -15.86) * mm});
            skLineSegment(sketch, "E130", {"start": v(-34, -15.86) * mm, "end": v(-33.58, -15.93) * mm});
            skLineSegment(sketch, "E131", {"start": v(-33.58, -15.93) * mm, "end": v(-33.14, -15.86) * mm});
            skLineSegment(sketch, "E132", {"start": v(-33.14, -15.86) * mm, "end": v(-32.75, -15.66) * mm});
            skLineSegment(sketch, "E133", {"start": v(-32.75, -15.66) * mm, "end": v(-32.44, -15.35) * mm});
            skLineSegment(sketch, "E134", {"start": v(-32.44, -15.35) * mm, "end": v(-32.24, -14.96) * mm});
            skLineSegment(sketch, "E135", {"start": v(-32.24, -14.96) * mm, "end": v(-32.18, -14.53) * mm});
            skLineSegment(sketch, "E136", {"start": v(-32.18, -14.53) * mm, "end": v(-32.24, -14.1) * mm});
            skLineSegment(sketch, "E137", {"start": v(-32.24, -14.1) * mm, "end": v(-32.44, -13.7) * mm});
            skLineSegment(sketch, "E138", {"start": v(-32.44, -13.7) * mm, "end": v(-32.75, -13.4) * mm});
            skLineSegment(sketch, "E139", {"start": v(-32.75, -13.4) * mm, "end": v(-33.14, -13.2) * mm});
            skLineSegment(sketch, "E140", {"start": v(-33.14, -13.2) * mm, "end": v(-33.58, -13.13) * mm});
            skLineSegment(sketch, "E141", {"start": v(-33.58, -13.13) * mm, "end": v(-34, -13.2) * mm});
            skLineSegment(sketch, "E142", {"start": v(-30.47, 11.42) * mm, "end": v(30.47, 11.42) * mm});
            skLineSegment(sketch, "E143", {"start": v(30.47, 11.42) * mm, "end": v(30.47, -11.43) * mm});
            skLineSegment(sketch, "E144", {"start": v(30.47, -11.43) * mm, "end": v(-30.47, -11.43) * mm});
            skLineSegment(sketch, "E145", {"start": v(-30.47, -11.43) * mm, "end": v(-30.47, 11.42) * mm});
            skLineSegment(sketch, "E146", {"start": v(33.14, 15.86) * mm, "end": v(32.75, 15.66) * mm});
            skLineSegment(sketch, "E147", {"start": v(32.75, 15.66) * mm, "end": v(32.44, 15.35) * mm});
            skLineSegment(sketch, "E148", {"start": v(32.44, 15.35) * mm, "end": v(32.24, 14.96) * mm});
            skLineSegment(sketch, "E149", {"start": v(32.24, 14.96) * mm, "end": v(32.18, 14.53) * mm});
            skLineSegment(sketch, "E150", {"start": v(32.18, 14.53) * mm, "end": v(32.24, 14.1) * mm});
            skLineSegment(sketch, "E151", {"start": v(32.24, 14.1) * mm, "end": v(32.44, 13.7) * mm});
            skLineSegment(sketch, "E152", {"start": v(32.44, 13.7) * mm, "end": v(32.75, 13.4) * mm});
            skLineSegment(sketch, "E153", {"start": v(32.75, 13.4) * mm, "end": v(33.14, 13.2) * mm});
            skLineSegment(sketch, "E154", {"start": v(33.14, 13.2) * mm, "end": v(33.58, 13.13) * mm});
            skLineSegment(sketch, "E155", {"start": v(33.58, 13.13) * mm, "end": v(34, 13.2) * mm});
            skLineSegment(sketch, "E156", {"start": v(34, 13.2) * mm, "end": v(34.4, 13.4) * mm});
            skLineSegment(sketch, "E157", {"start": v(34.4, 13.4) * mm, "end": v(34.7, 13.7) * mm});
            skLineSegment(sketch, "E158", {"start": v(34.7, 13.7) * mm, "end": v(34.9, 14.1) * mm});
            skLineSegment(sketch, "E159", {"start": v(34.9, 14.1) * mm, "end": v(34.98, 14.53) * mm});
            skLineSegment(sketch, "E160", {"start": v(34.98, 14.53) * mm, "end": v(34.9, 14.96) * mm});
            skLineSegment(sketch, "E161", {"start": v(34.9, 14.96) * mm, "end": v(34.7, 15.35) * mm});
            skLineSegment(sketch, "E162", {"start": v(34.7, 15.35) * mm, "end": v(34.4, 15.66) * mm});
            skLineSegment(sketch, "E163", {"start": v(34.4, 15.66) * mm, "end": v(34, 15.86) * mm});
            skLineSegment(sketch, "E164", {"start": v(34, 15.86) * mm, "end": v(33.58, 15.93) * mm});
            skLineSegment(sketch, "E165", {"start": v(33.58, 15.93) * mm, "end": v(33.14, 15.86) * mm});
            skLineSegment(sketch, "E166", {"start": v(-34, 15.86) * mm, "end": v(-34.4, 15.66) * mm});
            skLineSegment(sketch, "E167", {"start": v(-34.4, 15.66) * mm, "end": v(-34.7, 15.35) * mm});
            skLineSegment(sketch, "E168", {"start": v(-34.7, 15.35) * mm, "end": v(-34.9, 14.96) * mm});
            skLineSegment(sketch, "E169", {"start": v(-34.9, 14.96) * mm, "end": v(-34.98, 14.53) * mm});
            skLineSegment(sketch, "E170", {"start": v(-34.98, 14.53) * mm, "end": v(-34.9, 14.1) * mm});
            skLineSegment(sketch, "E171", {"start": v(-34.9, 14.1) * mm, "end": v(-34.7, 13.7) * mm});
            skLineSegment(sketch, "E172", {"start": v(-34.7, 13.7) * mm, "end": v(-34.4, 13.4) * mm});
            skLineSegment(sketch, "E173", {"start": v(-34.4, 13.4) * mm, "end": v(-34, 13.2) * mm});
            skLineSegment(sketch, "E174", {"start": v(-34, 13.2) * mm, "end": v(-33.58, 13.13) * mm});
            skLineSegment(sketch, "E175", {"start": v(-33.58, 13.13) * mm, "end": v(-33.14, 13.2) * mm});
            skLineSegment(sketch, "E176", {"start": v(-33.14, 13.2) * mm, "end": v(-32.75, 13.4) * mm});
            skLineSegment(sketch, "E177", {"start": v(-32.75, 13.4) * mm, "end": v(-32.44, 13.7) * mm});
            skLineSegment(sketch, "E178", {"start": v(-32.44, 13.7) * mm, "end": v(-32.24, 14.1) * mm});
            skLineSegment(sketch, "E179", {"start": v(-32.24, 14.1) * mm, "end": v(-32.18, 14.53) * mm});
            skLineSegment(sketch, "E180", {"start": v(-32.18, 14.53) * mm, "end": v(-32.24, 14.96) * mm});
            skLineSegment(sketch, "E181", {"start": v(-32.24, 14.96) * mm, "end": v(-32.44, 15.35) * mm});
            skLineSegment(sketch, "E182", {"start": v(-32.44, 15.35) * mm, "end": v(-32.75, 15.66) * mm});
            skLineSegment(sketch, "E183", {"start": v(-32.75, 15.66) * mm, "end": v(-33.14, 15.86) * mm});
            skLineSegment(sketch, "E184", {"start": v(-33.14, 15.86) * mm, "end": v(-33.58, 15.93) * mm});
            skLineSegment(sketch, "E185", {"start": v(-33.58, 15.93) * mm, "end": v(-34, 15.86) * mm});
            skSolve(sketch);
        }
        {
            var Q0;
            Q0 = qSketchRegion(id + "F3", true);
            extrude(context, id + "F4", {"entities" : qUnion([Q0]), "depth" : (getVariable(context, 'Thickness')) * mm, "offsetDistance" : 25 * mm});
        }
        {
            var Q0;
            Q0=makeQuery(id+"F4.opExtrude","CAP_FACE",FACE,{"disambiguationData":[OSD([sQuery(id+"F3.wireOp",EDGE,"E18"),sQuery(id+"F3.wireOp",EDGE,"E19"),sQuery(id+"F3.wireOp",EDGE,"E20"),sQuery(id+"F3.wireOp",EDGE,"E21"),sQuery(id+"F3.wireOp",EDGE,"E22"),sQuery(id+"F3.wireOp",EDGE,"E23"),sQuery(id+"F3.wireOp",EDGE,"E24"),sQuery(id+"F3.wireOp",EDGE,"E25"),sQuery(id+"F3.wireOp",EDGE,"E26"),sQuery(id+"F3.wireOp",EDGE,"E27"),sQuery(id+"F3.wireOp",EDGE,"E28"),sQuery(id+"F3.wireOp",EDGE,"E29"),sQuery(id+"F3.wireOp",EDGE,"E30"),sQuery(id+"F3.wireOp",EDGE,"E31"),sQuery(id+"F3.wireOp",EDGE,"E32"),sQuery(id+"F3.wireOp",EDGE,"E33"),sQuery(id+"F3.wireOp",EDGE,"E34"),sQuery(id+"F3.wireOp",EDGE,"E35"),sQuery(id+"F3.wireOp",EDGE,"E36"),sQuery(id+"F3.wireOp",EDGE,"E37"),sQuery(id+"F3.wireOp",EDGE,"E38"),sQuery(id+"F3.wireOp",EDGE,"E39"),sQuery(id+"F3.wireOp",EDGE,"E40"),sQuery(id+"F3.wireOp",EDGE,"E41"),sQuery(id+"F3.wireOp",EDGE,"E42"),sQuery(id+"F3.wireOp",EDGE,"E43"),sQuery(id+"F3.wireOp",EDGE,"E44"),sQuery(id+"F3.wireOp",EDGE,"E45"),sQuery(id+"F3.wireOp",EDGE,"E46"),sQuery(id+"F3.wireOp",EDGE,"E47"),sQuery(id+"F3.wireOp",EDGE,"E48"),sQuery(id+"F3.wireOp",EDGE,"E49"),sQuery(id+"F3.wireOp",EDGE,"E50"),sQuery(id+"F3.wireOp",EDGE,"E51"),sQuery(id+"F3.wireOp",EDGE,"E52"),sQuery(id+"F3.wireOp",EDGE,"E53"),sQuery(id+"F3.wireOp",EDGE,"E54"),sQuery(id+"F3.wireOp",EDGE,"E55"),sQuery(id+"F3.wireOp",EDGE,"E56"),sQuery(id+"F3.wireOp",EDGE,"E57"),sQuery(id+"F3.wireOp",EDGE,"E58"),sQuery(id+"F3.wireOp",EDGE,"E59"),sQuery(id+"F3.wireOp",EDGE,"E60"),sQuery(id+"F3.wireOp",EDGE,"E61"),sQuery(id+"F3.wireOp",EDGE,"E62"),sQuery(id+"F3.wireOp",EDGE,"E63"),sQuery(id+"F3.wireOp",EDGE,"E64"),sQuery(id+"F3.wireOp",EDGE,"E65"),sQuery(id+"F3.wireOp",EDGE,"E66"),sQuery(id+"F3.wireOp",EDGE,"E67"),sQuery(id+"F3.wireOp",EDGE,"E68"),sQuery(id+"F3.wireOp",EDGE,"E69"),sQuery(id+"F3.wireOp",EDGE,"E70"),sQuery(id+"F3.wireOp",EDGE,"E71"),sQuery(id+"F3.wireOp",EDGE,"E72"),sQuery(id+"F3.wireOp",EDGE,"E73"),sQuery(id+"F3.wireOp",EDGE,"E74"),sQuery(id+"F3.wireOp",EDGE,"E75"),sQuery(id+"F3.wireOp",EDGE,"E76"),sQuery(id+"F3.wireOp",EDGE,"E77"),sQuery(id+"F3.wireOp",EDGE,"E78"),sQuery(id+"F3.wireOp",EDGE,"E79"),sQuery(id+"F3.wireOp",EDGE,"E80"),sQuery(id+"F3.wireOp",EDGE,"E81"),sQuery(id+"F3.wireOp",EDGE,"E82"),sQuery(id+"F3.wireOp",EDGE,"E83"),sQuery(id+"F3.wireOp",EDGE,"E84"),sQuery(id+"F3.wireOp",EDGE,"E85"),sQuery(id+"F3.wireOp",EDGE,"E86"),sQuery(id+"F3.wireOp",EDGE,"E87"),sQuery(id+"F3.wireOp",EDGE,"E88"),sQuery(id+"F3.wireOp",EDGE,"E89"),sQuery(id+"F3.wireOp",EDGE,"E90"),sQuery(id+"F3.wireOp",EDGE,"E91"),sQuery(id+"F3.wireOp",EDGE,"E92"),sQuery(id+"F3.wireOp",EDGE,"E93"),sQuery(id+"F3.wireOp",EDGE,"E94"),sQuery(id+"F3.wireOp",EDGE,"E95"),sQuery(id+"F3.wireOp",EDGE,"E96"),sQuery(id+"F3.wireOp",EDGE,"E97"),sQuery(id+"F3.wireOp",EDGE,"E98"),sQuery(id+"F3.wireOp",EDGE,"E99"),sQuery(id+"F3.wireOp",EDGE,"E100"),sQuery(id+"F3.wireOp",EDGE,"E101"),sQuery(id+"F3.wireOp",EDGE,"E102"),sQuery(id+"F3.wireOp",EDGE,"E103"),sQuery(id+"F3.wireOp",EDGE,"E104"),sQuery(id+"F3.wireOp",EDGE,"E105"),sQuery(id+"F3.wireOp",EDGE,"E106"),sQuery(id+"F3.wireOp",EDGE,"E107"),sQuery(id+"F3.wireOp",EDGE,"E108"),sQuery(id+"F3.wireOp",EDGE,"E109"),sQuery(id+"F3.wireOp",EDGE,"E110"),sQuery(id+"F3.wireOp",EDGE,"E111"),sQuery(id+"F3.wireOp",EDGE,"E112"),sQuery(id+"F3.wireOp",EDGE,"E113"),sQuery(id+"F3.wireOp",EDGE,"E114"),sQuery(id+"F3.wireOp",EDGE,"E115"),sQuery(id+"F3.wireOp",EDGE,"E116"),sQuery(id+"F3.wireOp",EDGE,"E117"),sQuery(id+"F3.wireOp",EDGE,"E118"),sQuery(id+"F3.wireOp",EDGE,"E119"),sQuery(id+"F3.wireOp",EDGE,"E120"),sQuery(id+"F3.wireOp",EDGE,"E121"),sQuery(id+"F3.wireOp",EDGE,"E122"),sQuery(id+"F3.wireOp",EDGE,"E123"),sQuery(id+"F3.wireOp",EDGE,"E124"),sQuery(id+"F3.wireOp",EDGE,"E125"),sQuery(id+"F3.wireOp",EDGE,"E126"),sQuery(id+"F3.wireOp",EDGE,"E127"),sQuery(id+"F3.wireOp",EDGE,"E128"),sQuery(id+"F3.wireOp",EDGE,"E129"),sQuery(id+"F3.wireOp",EDGE,"E130"),sQuery(id+"F3.wireOp",EDGE,"E131"),sQuery(id+"F3.wireOp",EDGE,"E132"),sQuery(id+"F3.wireOp",EDGE,"E133"),sQuery(id+"F3.wireOp",EDGE,"E134"),sQuery(id+"F3.wireOp",EDGE,"E135"),sQuery(id+"F3.wireOp",EDGE,"E136"),sQuery(id+"F3.wireOp",EDGE,"E137"),sQuery(id+"F3.wireOp",EDGE,"E138"),sQuery(id+"F3.wireOp",EDGE,"E139"),sQuery(id+"F3.wireOp",EDGE,"E140"),sQuery(id+"F3.wireOp",EDGE,"E141"),sQuery(id+"F3.wireOp",EDGE,"E142"),sQuery(id+"F3.wireOp",EDGE,"E143"),sQuery(id+"F3.wireOp",EDGE,"E144"),sQuery(id+"F3.wireOp",EDGE,"E145"),sQuery(id+"F3.wireOp",EDGE,"E146"),sQuery(id+"F3.wireOp",EDGE,"E147"),sQuery(id+"F3.wireOp",EDGE,"E148"),sQuery(id+"F3.wireOp",EDGE,"E149"),sQuery(id+"F3.wireOp",EDGE,"E150"),sQuery(id+"F3.wireOp",EDGE,"E151"),sQuery(id+"F3.wireOp",EDGE,"E152"),sQuery(id+"F3.wireOp",EDGE,"E153"),sQuery(id+"F3.wireOp",EDGE,"E154"),sQuery(id+"F3.wireOp",EDGE,"E155"),sQuery(id+"F3.wireOp",EDGE,"E156"),sQuery(id+"F3.wireOp",EDGE,"E157"),sQuery(id+"F3.wireOp",EDGE,"E158"),sQuery(id+"F3.wireOp",EDGE,"E159"),sQuery(id+"F3.wireOp",EDGE,"E160"),sQuery(id+"F3.wireOp",EDGE,"E161"),sQuery(id+"F3.wireOp",EDGE,"E162"),sQuery(id+"F3.wireOp",EDGE,"E163"),sQuery(id+"F3.wireOp",EDGE,"E164"),sQuery(id+"F3.wireOp",EDGE,"E165"),sQuery(id+"F3.wireOp",EDGE,"E166"),sQuery(id+"F3.wireOp",EDGE,"E167"),sQuery(id+"F3.wireOp",EDGE,"E168"),sQuery(id+"F3.wireOp",EDGE,"E169"),sQuery(id+"F3.wireOp",EDGE,"E170"),sQuery(id+"F3.wireOp",EDGE,"E171"),sQuery(id+"F3.wireOp",EDGE,"E172"),sQuery(id+"F3.wireOp",EDGE,"E173"),sQuery(id+"F3.wireOp",EDGE,"E174"),sQuery(id+"F3.wireOp",EDGE,"E175"),sQuery(id+"F3.wireOp",EDGE,"E176"),sQuery(id+"F3.wireOp",EDGE,"E177"),sQuery(id+"F3.wireOp",EDGE,"E178"),sQuery(id+"F3.wireOp",EDGE,"E179"),sQuery(id+"F3.wireOp",EDGE,"E180"),sQuery(id+"F3.wireOp",EDGE,"E181"),sQuery(id+"F3.wireOp",EDGE,"E182"),sQuery(id+"F3.wireOp",EDGE,"E183"),sQuery(id+"F3.wireOp",EDGE,"E184"),sQuery(id+"F3.wireOp",EDGE,"E185")])],"isStart":false});
            var sketch = newSketch(context, id + "F5", { "sketchPlane" : qUnion([Q0])});
            skLineSegment(sketch, "E186", {"start": v(-4.9, 17.63) * mm, "end": v(-4.9, 11.42) * mm});
            skLineSegment(sketch, "E187", {"start": v(-4.9, 11.42) * mm, "end": v(-30.47, 11.42) * mm});
            skLineSegment(sketch, "E188", {"start": v(-30.47, 11.42) * mm, "end": v(-30.47, -11.43) * mm});
            skLineSegment(sketch, "E189", {"start": v(-30.47, -11.43) * mm, "end": v(30.47, -11.43) * mm});
            skLineSegment(sketch, "E190", {"start": v(30.47, -11.43) * mm, "end": v(30.47, 11.42) * mm});
            skLineSegment(sketch, "E191", {"start": v(30.47, 11.42) * mm, "end": v(4.9, 11.42) * mm});
            skLineSegment(sketch, "E192", {"start": v(4.9, 11.42) * mm, "end": v(4.9, 17.62) * mm});
            skLineSegment(sketch, "E193", {"start": v(4.9, 17.62) * mm, "end": v(34.68, 17.62) * mm});
            skLineSegment(sketch, "E194", {"start": v(34.68, 17.62) * mm, "end": v(34.83, 17.62) * mm});
            skLineSegment(sketch, "E195", {"start": v(34.83, 17.62) * mm, "end": v(34.99, 17.6) * mm});
            skLineSegment(sketch, "E196", {"start": v(34.99, 17.6) * mm, "end": v(35.14, 17.57) * mm});
            skLineSegment(sketch, "E197", {"start": v(35.14, 17.57) * mm, "end": v(35.3, 17.53) * mm});
            skLineSegment(sketch, "E198", {"start": v(35.3, 17.53) * mm, "end": v(35.44, 17.47) * mm});
            skLineSegment(sketch, "E199", {"start": v(35.44, 17.47) * mm, "end": v(35.58, 17.4) * mm});
            skLineSegment(sketch, "E200", {"start": v(35.58, 17.4) * mm, "end": v(35.72, 17.33) * mm});
            skLineSegment(sketch, "E201", {"start": v(35.72, 17.33) * mm, "end": v(35.85, 17.24) * mm});
            skLineSegment(sketch, "E202", {"start": v(35.85, 17.24) * mm, "end": v(35.97, 17.15) * mm});
            skLineSegment(sketch, "E203", {"start": v(35.97, 17.15) * mm, "end": v(36.1, 17.04) * mm});
            skLineSegment(sketch, "E204", {"start": v(36.1, 17.04) * mm, "end": v(36.2, 16.92) * mm});
            skLineSegment(sketch, "E205", {"start": v(36.2, 16.92) * mm, "end": v(36.3, 16.8) * mm});
            skLineSegment(sketch, "E206", {"start": v(36.3, 16.8) * mm, "end": v(36.38, 16.67) * mm});
            skLineSegment(sketch, "E207", {"start": v(36.38, 16.67) * mm, "end": v(36.46, 16.53) * mm});
            skLineSegment(sketch, "E208", {"start": v(36.46, 16.53) * mm, "end": v(36.52, 16.4) * mm});
            skLineSegment(sketch, "E209", {"start": v(36.52, 16.4) * mm, "end": v(36.58, 16.24) * mm});
            skLineSegment(sketch, "E210", {"start": v(36.58, 16.24) * mm, "end": v(36.62, 16.1) * mm});
            skLineSegment(sketch, "E211", {"start": v(36.62, 16.1) * mm, "end": v(36.65, 15.94) * mm});
            skLineSegment(sketch, "E212", {"start": v(36.65, 15.94) * mm, "end": v(36.67, 15.78) * mm});
            skLineSegment(sketch, "E213", {"start": v(36.67, 15.78) * mm, "end": v(36.68, 15.62) * mm});
            skLineSegment(sketch, "E214", {"start": v(36.68, 15.62) * mm, "end": v(36.68, -15.63) * mm});
            skLineSegment(sketch, "E215", {"start": v(36.68, -15.63) * mm, "end": v(36.67, -15.78) * mm});
            skLineSegment(sketch, "E216", {"start": v(36.67, -15.78) * mm, "end": v(36.65, -15.94) * mm});
            skLineSegment(sketch, "E217", {"start": v(36.65, -15.94) * mm, "end": v(36.62, -16.1) * mm});
            skLineSegment(sketch, "E218", {"start": v(36.62, -16.1) * mm, "end": v(36.58, -16.24) * mm});
            skLineSegment(sketch, "E219", {"start": v(36.58, -16.24) * mm, "end": v(36.52, -16.4) * mm});
            skLineSegment(sketch, "E220", {"start": v(36.52, -16.4) * mm, "end": v(36.46, -16.53) * mm});
            skLineSegment(sketch, "E221", {"start": v(36.46, -16.53) * mm, "end": v(36.38, -16.67) * mm});
            skLineSegment(sketch, "E222", {"start": v(36.38, -16.67) * mm, "end": v(36.3, -16.8) * mm});
            skLineSegment(sketch, "E223", {"start": v(36.3, -16.8) * mm, "end": v(36.2, -16.92) * mm});
            skLineSegment(sketch, "E224", {"start": v(36.2, -16.92) * mm, "end": v(36.1, -17.04) * mm});
            skLineSegment(sketch, "E225", {"start": v(36.1, -17.04) * mm, "end": v(35.97, -17.15) * mm});
            skLineSegment(sketch, "E226", {"start": v(35.97, -17.15) * mm, "end": v(35.85, -17.24) * mm});
            skLineSegment(sketch, "E227", {"start": v(35.85, -17.24) * mm, "end": v(35.72, -17.33) * mm});
            skLineSegment(sketch, "E228", {"start": v(35.72, -17.33) * mm, "end": v(35.58, -17.4) * mm});
            skLineSegment(sketch, "E229", {"start": v(35.58, -17.4) * mm, "end": v(35.44, -17.47) * mm});
            skLineSegment(sketch, "E230", {"start": v(35.44, -17.47) * mm, "end": v(35.3, -17.53) * mm});
            skLineSegment(sketch, "E231", {"start": v(35.3, -17.53) * mm, "end": v(35.14, -17.57) * mm});
            skLineSegment(sketch, "E232", {"start": v(35.14, -17.57) * mm, "end": v(34.99, -17.6) * mm});
            skLineSegment(sketch, "E233", {"start": v(34.99, -17.6) * mm, "end": v(34.83, -17.62) * mm});
            skLineSegment(sketch, "E234", {"start": v(34.83, -17.62) * mm, "end": v(34.68, -17.63) * mm});
            skLineSegment(sketch, "E235", {"start": v(34.68, -17.63) * mm, "end": v(-34.67, -17.63) * mm});
            skLineSegment(sketch, "E236", {"start": v(-34.67, -17.63) * mm, "end": v(-34.83, -17.62) * mm});
            skLineSegment(sketch, "E237", {"start": v(-34.83, -17.62) * mm, "end": v(-34.99, -17.6) * mm});
            skLineSegment(sketch, "E238", {"start": v(-34.99, -17.6) * mm, "end": v(-35.14, -17.57) * mm});
            skLineSegment(sketch, "E239", {"start": v(-35.14, -17.57) * mm, "end": v(-35.3, -17.53) * mm});
            skLineSegment(sketch, "E240", {"start": v(-35.3, -17.53) * mm, "end": v(-35.44, -17.47) * mm});
            skLineSegment(sketch, "E241", {"start": v(-35.44, -17.47) * mm, "end": v(-35.58, -17.4) * mm});
            skLineSegment(sketch, "E242", {"start": v(-35.58, -17.4) * mm, "end": v(-35.72, -17.33) * mm});
            skLineSegment(sketch, "E243", {"start": v(-35.72, -17.33) * mm, "end": v(-35.85, -17.24) * mm});
            skLineSegment(sketch, "E244", {"start": v(-35.85, -17.24) * mm, "end": v(-35.97, -17.15) * mm});
            skLineSegment(sketch, "E245", {"start": v(-35.97, -17.15) * mm, "end": v(-36.1, -17.04) * mm});
            skLineSegment(sketch, "E246", {"start": v(-36.1, -17.04) * mm, "end": v(-36.2, -16.92) * mm});
            skLineSegment(sketch, "E247", {"start": v(-36.2, -16.92) * mm, "end": v(-36.3, -16.8) * mm});
            skLineSegment(sketch, "E248", {"start": v(-36.3, -16.8) * mm, "end": v(-36.38, -16.67) * mm});
            skLineSegment(sketch, "E249", {"start": v(-36.38, -16.67) * mm, "end": v(-36.46, -16.53) * mm});
            skLineSegment(sketch, "E250", {"start": v(-36.46, -16.53) * mm, "end": v(-36.52, -16.4) * mm});
            skLineSegment(sketch, "E251", {"start": v(-36.52, -16.4) * mm, "end": v(-36.58, -16.24) * mm});
            skLineSegment(sketch, "E252", {"start": v(-36.58, -16.24) * mm, "end": v(-36.62, -16.1) * mm});
            skLineSegment(sketch, "E253", {"start": v(-36.62, -16.1) * mm, "end": v(-36.65, -15.94) * mm});
            skLineSegment(sketch, "E254", {"start": v(-36.65, -15.94) * mm, "end": v(-36.67, -15.78) * mm});
            skLineSegment(sketch, "E255", {"start": v(-36.67, -15.78) * mm, "end": v(-36.68, -15.62) * mm});
            skLineSegment(sketch, "E256", {"start": v(-36.68, -15.62) * mm, "end": v(-36.67, 15.62) * mm});
            skLineSegment(sketch, "E257", {"start": v(-36.67, 15.62) * mm, "end": v(-36.67, 15.78) * mm});
            skLineSegment(sketch, "E258", {"start": v(-36.67, 15.78) * mm, "end": v(-36.65, 15.94) * mm});
            skLineSegment(sketch, "E259", {"start": v(-36.65, 15.94) * mm, "end": v(-36.62, 16.1) * mm});
            skLineSegment(sketch, "E260", {"start": v(-36.62, 16.1) * mm, "end": v(-36.58, 16.24) * mm});
            skLineSegment(sketch, "E261", {"start": v(-36.58, 16.24) * mm, "end": v(-36.52, 16.4) * mm});
            skLineSegment(sketch, "E262", {"start": v(-36.52, 16.4) * mm, "end": v(-36.46, 16.53) * mm});
            skLineSegment(sketch, "E263", {"start": v(-36.46, 16.53) * mm, "end": v(-36.38, 16.67) * mm});
            skLineSegment(sketch, "E264", {"start": v(-36.38, 16.67) * mm, "end": v(-36.3, 16.8) * mm});
            skLineSegment(sketch, "E265", {"start": v(-36.3, 16.8) * mm, "end": v(-36.2, 16.92) * mm});
            skLineSegment(sketch, "E266", {"start": v(-36.2, 16.92) * mm, "end": v(-36.1, 17.04) * mm});
            skLineSegment(sketch, "E267", {"start": v(-36.1, 17.04) * mm, "end": v(-35.97, 17.15) * mm});
            skLineSegment(sketch, "E268", {"start": v(-35.97, 17.15) * mm, "end": v(-35.85, 17.24) * mm});
            skLineSegment(sketch, "E269", {"start": v(-35.85, 17.24) * mm, "end": v(-35.72, 17.33) * mm});
            skLineSegment(sketch, "E270", {"start": v(-35.72, 17.33) * mm, "end": v(-35.58, 17.4) * mm});
            skLineSegment(sketch, "E271", {"start": v(-35.58, 17.4) * mm, "end": v(-35.44, 17.47) * mm});
            skLineSegment(sketch, "E272", {"start": v(-35.44, 17.47) * mm, "end": v(-35.3, 17.53) * mm});
            skLineSegment(sketch, "E273", {"start": v(-35.3, 17.53) * mm, "end": v(-35.14, 17.57) * mm});
            skLineSegment(sketch, "E274", {"start": v(-35.14, 17.57) * mm, "end": v(-34.99, 17.6) * mm});
            skLineSegment(sketch, "E275", {"start": v(-34.99, 17.6) * mm, "end": v(-34.83, 17.62) * mm});
            skLineSegment(sketch, "E276", {"start": v(-34.83, 17.62) * mm, "end": v(-34.67, 17.63) * mm});
            skLineSegment(sketch, "E277", {"start": v(-34.67, 17.63) * mm, "end": v(-4.9, 17.63) * mm});
            skLineSegment(sketch, "E278", {"start": v(33.14, -13.2) * mm, "end": v(32.75, -13.4) * mm});
            skLineSegment(sketch, "E279", {"start": v(32.75, -13.4) * mm, "end": v(32.44, -13.7) * mm});
            skLineSegment(sketch, "E280", {"start": v(32.44, -13.7) * mm, "end": v(32.24, -14.1) * mm});
            skLineSegment(sketch, "E281", {"start": v(32.24, -14.1) * mm, "end": v(32.18, -14.53) * mm});
            skLineSegment(sketch, "E282", {"start": v(32.18, -14.53) * mm, "end": v(32.24, -14.96) * mm});
            skLineSegment(sketch, "E283", {"start": v(32.24, -14.96) * mm, "end": v(32.44, -15.35) * mm});
            skLineSegment(sketch, "E284", {"start": v(32.44, -15.35) * mm, "end": v(32.75, -15.66) * mm});
            skLineSegment(sketch, "E285", {"start": v(32.75, -15.66) * mm, "end": v(33.14, -15.86) * mm});
            skLineSegment(sketch, "E286", {"start": v(33.14, -15.86) * mm, "end": v(33.58, -15.93) * mm});
            skLineSegment(sketch, "E287", {"start": v(33.58, -15.93) * mm, "end": v(34, -15.86) * mm});
            skLineSegment(sketch, "E288", {"start": v(34, -15.86) * mm, "end": v(34.4, -15.66) * mm});
            skLineSegment(sketch, "E289", {"start": v(34.4, -15.66) * mm, "end": v(34.7, -15.35) * mm});
            skLineSegment(sketch, "E290", {"start": v(34.7, -15.35) * mm, "end": v(34.9, -14.96) * mm});
            skLineSegment(sketch, "E291", {"start": v(34.9, -14.96) * mm, "end": v(34.98, -14.53) * mm});
            skLineSegment(sketch, "E292", {"start": v(34.98, -14.53) * mm, "end": v(34.9, -14.1) * mm});
            skLineSegment(sketch, "E293", {"start": v(34.9, -14.1) * mm, "end": v(34.7, -13.7) * mm});
            skLineSegment(sketch, "E294", {"start": v(34.7, -13.7) * mm, "end": v(34.4, -13.4) * mm});
            skLineSegment(sketch, "E295", {"start": v(34.4, -13.4) * mm, "end": v(34, -13.2) * mm});
            skLineSegment(sketch, "E296", {"start": v(34, -13.2) * mm, "end": v(33.58, -13.13) * mm});
            skLineSegment(sketch, "E297", {"start": v(33.58, -13.13) * mm, "end": v(33.14, -13.2) * mm});
            skLineSegment(sketch, "E298", {"start": v(-34, -13.2) * mm, "end": v(-34.4, -13.4) * mm});
            skLineSegment(sketch, "E299", {"start": v(-34.4, -13.4) * mm, "end": v(-34.7, -13.7) * mm});
            skLineSegment(sketch, "E300", {"start": v(-34.7, -13.7) * mm, "end": v(-34.9, -14.1) * mm});
            skLineSegment(sketch, "E301", {"start": v(-34.9, -14.1) * mm, "end": v(-34.98, -14.53) * mm});
            skLineSegment(sketch, "E302", {"start": v(-34.98, -14.53) * mm, "end": v(-34.9, -14.96) * mm});
            skLineSegment(sketch, "E303", {"start": v(-34.9, -14.96) * mm, "end": v(-34.7, -15.35) * mm});
            skLineSegment(sketch, "E304", {"start": v(-34.7, -15.35) * mm, "end": v(-34.4, -15.66) * mm});
            skLineSegment(sketch, "E305", {"start": v(-34.4, -15.66) * mm, "end": v(-34, -15.86) * mm});
            skLineSegment(sketch, "E306", {"start": v(-34, -15.86) * mm, "end": v(-33.58, -15.93) * mm});
            skLineSegment(sketch, "E307", {"start": v(-33.58, -15.93) * mm, "end": v(-33.14, -15.86) * mm});
            skLineSegment(sketch, "E308", {"start": v(-33.14, -15.86) * mm, "end": v(-32.75, -15.66) * mm});
            skLineSegment(sketch, "E309", {"start": v(-32.75, -15.66) * mm, "end": v(-32.44, -15.35) * mm});
            skLineSegment(sketch, "E310", {"start": v(-32.44, -15.35) * mm, "end": v(-32.24, -14.96) * mm});
            skLineSegment(sketch, "E311", {"start": v(-32.24, -14.96) * mm, "end": v(-32.18, -14.53) * mm});
            skLineSegment(sketch, "E312", {"start": v(-32.18, -14.53) * mm, "end": v(-32.24, -14.1) * mm});
            skLineSegment(sketch, "E313", {"start": v(-32.24, -14.1) * mm, "end": v(-32.44, -13.7) * mm});
            skLineSegment(sketch, "E314", {"start": v(-32.44, -13.7) * mm, "end": v(-32.75, -13.4) * mm});
            skLineSegment(sketch, "E315", {"start": v(-32.75, -13.4) * mm, "end": v(-33.14, -13.2) * mm});
            skLineSegment(sketch, "E316", {"start": v(-33.14, -13.2) * mm, "end": v(-33.58, -13.13) * mm});
            skLineSegment(sketch, "E317", {"start": v(-33.58, -13.13) * mm, "end": v(-34, -13.2) * mm});
            skLineSegment(sketch, "E318", {"start": v(33.14, 15.86) * mm, "end": v(32.75, 15.66) * mm});
            skLineSegment(sketch, "E319", {"start": v(32.75, 15.66) * mm, "end": v(32.44, 15.35) * mm});
            skLineSegment(sketch, "E320", {"start": v(32.44, 15.35) * mm, "end": v(32.24, 14.96) * mm});
            skLineSegment(sketch, "E321", {"start": v(32.24, 14.96) * mm, "end": v(32.18, 14.53) * mm});
            skLineSegment(sketch, "E322", {"start": v(32.18, 14.53) * mm, "end": v(32.24, 14.1) * mm});
            skLineSegment(sketch, "E323", {"start": v(32.24, 14.1) * mm, "end": v(32.44, 13.7) * mm});
            skLineSegment(sketch, "E324", {"start": v(32.44, 13.7) * mm, "end": v(32.75, 13.4) * mm});
            skLineSegment(sketch, "E325", {"start": v(32.75, 13.4) * mm, "end": v(33.14, 13.2) * mm});
            skLineSegment(sketch, "E326", {"start": v(33.14, 13.2) * mm, "end": v(33.58, 13.13) * mm});
            skLineSegment(sketch, "E327", {"start": v(33.58, 13.13) * mm, "end": v(34, 13.2) * mm});
            skLineSegment(sketch, "E328", {"start": v(34, 13.2) * mm, "end": v(34.4, 13.4) * mm});
            skLineSegment(sketch, "E329", {"start": v(34.4, 13.4) * mm, "end": v(34.7, 13.7) * mm});
            skLineSegment(sketch, "E330", {"start": v(34.7, 13.7) * mm, "end": v(34.9, 14.1) * mm});
            skLineSegment(sketch, "E331", {"start": v(34.9, 14.1) * mm, "end": v(34.98, 14.53) * mm});
            skLineSegment(sketch, "E332", {"start": v(34.98, 14.53) * mm, "end": v(34.9, 14.96) * mm});
            skLineSegment(sketch, "E333", {"start": v(34.9, 14.96) * mm, "end": v(34.7, 15.35) * mm});
            skLineSegment(sketch, "E334", {"start": v(34.7, 15.35) * mm, "end": v(34.4, 15.66) * mm});
            skLineSegment(sketch, "E335", {"start": v(34.4, 15.66) * mm, "end": v(34, 15.86) * mm});
            skLineSegment(sketch, "E336", {"start": v(34, 15.86) * mm, "end": v(33.58, 15.93) * mm});
            skLineSegment(sketch, "E337", {"start": v(33.58, 15.93) * mm, "end": v(33.14, 15.86) * mm});
            skLineSegment(sketch, "E338", {"start": v(-34, 15.86) * mm, "end": v(-34.4, 15.66) * mm});
            skLineSegment(sketch, "E339", {"start": v(-34.4, 15.66) * mm, "end": v(-34.7, 15.35) * mm});
            skLineSegment(sketch, "E340", {"start": v(-34.7, 15.35) * mm, "end": v(-34.9, 14.96) * mm});
            skLineSegment(sketch, "E341", {"start": v(-34.9, 14.96) * mm, "end": v(-34.98, 14.53) * mm});
            skLineSegment(sketch, "E342", {"start": v(-34.98, 14.53) * mm, "end": v(-34.9, 14.1) * mm});
            skLineSegment(sketch, "E343", {"start": v(-34.9, 14.1) * mm, "end": v(-34.7, 13.7) * mm});
            skLineSegment(sketch, "E344", {"start": v(-34.7, 13.7) * mm, "end": v(-34.4, 13.4) * mm});
            skLineSegment(sketch, "E345", {"start": v(-34.4, 13.4) * mm, "end": v(-34, 13.2) * mm});
            skLineSegment(sketch, "E346", {"start": v(-34, 13.2) * mm, "end": v(-33.58, 13.13) * mm});
            skLineSegment(sketch, "E347", {"start": v(-33.58, 13.13) * mm, "end": v(-33.14, 13.2) * mm});
            skLineSegment(sketch, "E348", {"start": v(-33.14, 13.2) * mm, "end": v(-32.75, 13.4) * mm});
            skLineSegment(sketch, "E349", {"start": v(-32.75, 13.4) * mm, "end": v(-32.44, 13.7) * mm});
            skLineSegment(sketch, "E350", {"start": v(-32.44, 13.7) * mm, "end": v(-32.24, 14.1) * mm});
            skLineSegment(sketch, "E351", {"start": v(-32.24, 14.1) * mm, "end": v(-32.18, 14.53) * mm});
            skLineSegment(sketch, "E352", {"start": v(-32.18, 14.53) * mm, "end": v(-32.24, 14.96) * mm});
            skLineSegment(sketch, "E353", {"start": v(-32.24, 14.96) * mm, "end": v(-32.44, 15.35) * mm});
            skLineSegment(sketch, "E354", {"start": v(-32.44, 15.35) * mm, "end": v(-32.75, 15.66) * mm});
            skLineSegment(sketch, "E355", {"start": v(-32.75, 15.66) * mm, "end": v(-33.14, 15.86) * mm});
            skLineSegment(sketch, "E356", {"start": v(-33.14, 15.86) * mm, "end": v(-33.58, 15.93) * mm});
            skLineSegment(sketch, "E357", {"start": v(-33.58, 15.93) * mm, "end": v(-34, 15.86) * mm});
            skSolve(sketch);
        }
        {
            var Q0;
            Q0 = qSketchRegion(id + "F5", true);
            extrude(context, id + "F6", {"entities" : qUnion([Q0]), "depth" : (getVariable(context, 'Thickness') * 2) * mm, "offsetDistance" : 25 * mm});
        }
        {
            var Q0;
            Q0=makeQuery(id+"F6.opExtrude","CAP_FACE",FACE,{"disambiguationData":[OSD([sQuery(id+"F5.wireOp",EDGE,"E186"),sQuery(id+"F5.wireOp",EDGE,"E187"),sQuery(id+"F5.wireOp",EDGE,"E188"),sQuery(id+"F5.wireOp",EDGE,"E189"),sQuery(id+"F5.wireOp",EDGE,"E190"),sQuery(id+"F5.wireOp",EDGE,"E191"),sQuery(id+"F5.wireOp",EDGE,"E192"),sQuery(id+"F5.wireOp",EDGE,"E193"),sQuery(id+"F5.wireOp",EDGE,"E194"),sQuery(id+"F5.wireOp",EDGE,"E195"),sQuery(id+"F5.wireOp",EDGE,"E196"),sQuery(id+"F5.wireOp",EDGE,"E197"),sQuery(id+"F5.wireOp",EDGE,"E198"),sQuery(id+"F5.wireOp",EDGE,"E199"),sQuery(id+"F5.wireOp",EDGE,"E200"),sQuery(id+"F5.wireOp",EDGE,"E201"),sQuery(id+"F5.wireOp",EDGE,"E202"),sQuery(id+"F5.wireOp",EDGE,"E203"),sQuery(id+"F5.wireOp",EDGE,"E204"),sQuery(id+"F5.wireOp",EDGE,"E205"),sQuery(id+"F5.wireOp",EDGE,"E206"),sQuery(id+"F5.wireOp",EDGE,"E207"),sQuery(id+"F5.wireOp",EDGE,"E208"),sQuery(id+"F5.wireOp",EDGE,"E209"),sQuery(id+"F5.wireOp",EDGE,"E210"),sQuery(id+"F5.wireOp",EDGE,"E211"),sQuery(id+"F5.wireOp",EDGE,"E212"),sQuery(id+"F5.wireOp",EDGE,"E213"),sQuery(id+"F5.wireOp",EDGE,"E214"),sQuery(id+"F5.wireOp",EDGE,"E215"),sQuery(id+"F5.wireOp",EDGE,"E216"),sQuery(id+"F5.wireOp",EDGE,"E217"),sQuery(id+"F5.wireOp",EDGE,"E218"),sQuery(id+"F5.wireOp",EDGE,"E219"),sQuery(id+"F5.wireOp",EDGE,"E220"),sQuery(id+"F5.wireOp",EDGE,"E221"),sQuery(id+"F5.wireOp",EDGE,"E222"),sQuery(id+"F5.wireOp",EDGE,"E223"),sQuery(id+"F5.wireOp",EDGE,"E224"),sQuery(id+"F5.wireOp",EDGE,"E225"),sQuery(id+"F5.wireOp",EDGE,"E226"),sQuery(id+"F5.wireOp",EDGE,"E227"),sQuery(id+"F5.wireOp",EDGE,"E228"),sQuery(id+"F5.wireOp",EDGE,"E229"),sQuery(id+"F5.wireOp",EDGE,"E230"),sQuery(id+"F5.wireOp",EDGE,"E231"),sQuery(id+"F5.wireOp",EDGE,"E232"),sQuery(id+"F5.wireOp",EDGE,"E233"),sQuery(id+"F5.wireOp",EDGE,"E234"),sQuery(id+"F5.wireOp",EDGE,"E235"),sQuery(id+"F5.wireOp",EDGE,"E236"),sQuery(id+"F5.wireOp",EDGE,"E237"),sQuery(id+"F5.wireOp",EDGE,"E238"),sQuery(id+"F5.wireOp",EDGE,"E239"),sQuery(id+"F5.wireOp",EDGE,"E240"),sQuery(id+"F5.wireOp",EDGE,"E241"),sQuery(id+"F5.wireOp",EDGE,"E242"),sQuery(id+"F5.wireOp",EDGE,"E243"),sQuery(id+"F5.wireOp",EDGE,"E244"),sQuery(id+"F5.wireOp",EDGE,"E245"),sQuery(id+"F5.wireOp",EDGE,"E246"),sQuery(id+"F5.wireOp",EDGE,"E247"),sQuery(id+"F5.wireOp",EDGE,"E248"),sQuery(id+"F5.wireOp",EDGE,"E249"),sQuery(id+"F5.wireOp",EDGE,"E250"),sQuery(id+"F5.wireOp",EDGE,"E251"),sQuery(id+"F5.wireOp",EDGE,"E252"),sQuery(id+"F5.wireOp",EDGE,"E253"),sQuery(id+"F5.wireOp",EDGE,"E254"),sQuery(id+"F5.wireOp",EDGE,"E255"),sQuery(id+"F5.wireOp",EDGE,"E256"),sQuery(id+"F5.wireOp",EDGE,"E257"),sQuery(id+"F5.wireOp",EDGE,"E258"),sQuery(id+"F5.wireOp",EDGE,"E259"),sQuery(id+"F5.wireOp",EDGE,"E260"),sQuery(id+"F5.wireOp",EDGE,"E261"),sQuery(id+"F5.wireOp",EDGE,"E262"),sQuery(id+"F5.wireOp",EDGE,"E263"),sQuery(id+"F5.wireOp",EDGE,"E264"),sQuery(id+"F5.wireOp",EDGE,"E265"),sQuery(id+"F5.wireOp",EDGE,"E266"),sQuery(id+"F5.wireOp",EDGE,"E267"),sQuery(id+"F5.wireOp",EDGE,"E268"),sQuery(id+"F5.wireOp",EDGE,"E269"),sQuery(id+"F5.wireOp",EDGE,"E270"),sQuery(id+"F5.wireOp",EDGE,"E271"),sQuery(id+"F5.wireOp",EDGE,"E272"),sQuery(id+"F5.wireOp",EDGE,"E273"),sQuery(id+"F5.wireOp",EDGE,"E274"),sQuery(id+"F5.wireOp",EDGE,"E275"),sQuery(id+"F5.wireOp",EDGE,"E276"),sQuery(id+"F5.wireOp",EDGE,"E277"),sQuery(id+"F5.wireOp",EDGE,"E278"),sQuery(id+"F5.wireOp",EDGE,"E279"),sQuery(id+"F5.wireOp",EDGE,"E280"),sQuery(id+"F5.wireOp",EDGE,"E281"),sQuery(id+"F5.wireOp",EDGE,"E282"),sQuery(id+"F5.wireOp",EDGE,"E283"),sQuery(id+"F5.wireOp",EDGE,"E284"),sQuery(id+"F5.wireOp",EDGE,"E285"),sQuery(id+"F5.wireOp",EDGE,"E286"),sQuery(id+"F5.wireOp",EDGE,"E287"),sQuery(id+"F5.wireOp",EDGE,"E288"),sQuery(id+"F5.wireOp",EDGE,"E289"),sQuery(id+"F5.wireOp",EDGE,"E290"),sQuery(id+"F5.wireOp",EDGE,"E291"),sQuery(id+"F5.wireOp",EDGE,"E292"),sQuery(id+"F5.wireOp",EDGE,"E293"),sQuery(id+"F5.wireOp",EDGE,"E294"),sQuery(id+"F5.wireOp",EDGE,"E295"),sQuery(id+"F5.wireOp",EDGE,"E296"),sQuery(id+"F5.wireOp",EDGE,"E297"),sQuery(id+"F5.wireOp",EDGE,"E298"),sQuery(id+"F5.wireOp",EDGE,"E299"),sQuery(id+"F5.wireOp",EDGE,"E300"),sQuery(id+"F5.wireOp",EDGE,"E301"),sQuery(id+"F5.wireOp",EDGE,"E302"),sQuery(id+"F5.wireOp",EDGE,"E303"),sQuery(id+"F5.wireOp",EDGE,"E304"),sQuery(id+"F5.wireOp",EDGE,"E305"),sQuery(id+"F5.wireOp",EDGE,"E306"),sQuery(id+"F5.wireOp",EDGE,"E307"),sQuery(id+"F5.wireOp",EDGE,"E308"),sQuery(id+"F5.wireOp",EDGE,"E309"),sQuery(id+"F5.wireOp",EDGE,"E310"),sQuery(id+"F5.wireOp",EDGE,"E311"),sQuery(id+"F5.wireOp",EDGE,"E312"),sQuery(id+"F5.wireOp",EDGE,"E313"),sQuery(id+"F5.wireOp",EDGE,"E314"),sQuery(id+"F5.wireOp",EDGE,"E315"),sQuery(id+"F5.wireOp",EDGE,"E316"),sQuery(id+"F5.wireOp",EDGE,"E317"),sQuery(id+"F5.wireOp",EDGE,"E318"),sQuery(id+"F5.wireOp",EDGE,"E319"),sQuery(id+"F5.wireOp",EDGE,"E320"),sQuery(id+"F5.wireOp",EDGE,"E321"),sQuery(id+"F5.wireOp",EDGE,"E322"),sQuery(id+"F5.wireOp",EDGE,"E323"),sQuery(id+"F5.wireOp",EDGE,"E324"),sQuery(id+"F5.wireOp",EDGE,"E325"),sQuery(id+"F5.wireOp",EDGE,"E326"),sQuery(id+"F5.wireOp",EDGE,"E327"),sQuery(id+"F5.wireOp",EDGE,"E328"),sQuery(id+"F5.wireOp",EDGE,"E329"),sQuery(id+"F5.wireOp",EDGE,"E330"),sQuery(id+"F5.wireOp",EDGE,"E331"),sQuery(id+"F5.wireOp",EDGE,"E332"),sQuery(id+"F5.wireOp",EDGE,"E333"),sQuery(id+"F5.wireOp",EDGE,"E334"),sQuery(id+"F5.wireOp",EDGE,"E335"),sQuery(id+"F5.wireOp",EDGE,"E336"),sQuery(id+"F5.wireOp",EDGE,"E337"),sQuery(id+"F5.wireOp",EDGE,"E338"),sQuery(id+"F5.wireOp",EDGE,"E339"),sQuery(id+"F5.wireOp",EDGE,"E340"),sQuery(id+"F5.wireOp",EDGE,"E341"),sQuery(id+"F5.wireOp",EDGE,"E342"),sQuery(id+"F5.wireOp",EDGE,"E343"),sQuery(id+"F5.wireOp",EDGE,"E344"),sQuery(id+"F5.wireOp",EDGE,"E345"),sQuery(id+"F5.wireOp",EDGE,"E346"),sQuery(id+"F5.wireOp",EDGE,"E347"),sQuery(id+"F5.wireOp",EDGE,"E348"),sQuery(id+"F5.wireOp",EDGE,"E349"),sQuery(id+"F5.wireOp",EDGE,"E350"),sQuery(id+"F5.wireOp",EDGE,"E351"),sQuery(id+"F5.wireOp",EDGE,"E352"),sQuery(id+"F5.wireOp",EDGE,"E353"),sQuery(id+"F5.wireOp",EDGE,"E354"),sQuery(id+"F5.wireOp",EDGE,"E355"),sQuery(id+"F5.wireOp",EDGE,"E356"),sQuery(id+"F5.wireOp",EDGE,"E357")])],"isStart":false});
            var sketch = newSketch(context, id + "F7", { "sketchPlane" : qUnion([Q0])});
            skLineSegment(sketch, "E358", {"start": v(34.68, 17.62) * mm, "end": v(34.83, 17.62) * mm});
            skLineSegment(sketch, "E359", {"start": v(34.83, 17.62) * mm, "end": v(34.99, 17.6) * mm});
            skLineSegment(sketch, "E360", {"start": v(34.99, 17.6) * mm, "end": v(35.14, 17.57) * mm});
            skLineSegment(sketch, "E361", {"start": v(35.14, 17.57) * mm, "end": v(35.3, 17.53) * mm});
            skLineSegment(sketch, "E362", {"start": v(35.3, 17.53) * mm, "end": v(35.44, 17.47) * mm});
            skLineSegment(sketch, "E363", {"start": v(35.44, 17.47) * mm, "end": v(35.58, 17.4) * mm});
            skLineSegment(sketch, "E364", {"start": v(35.58, 17.4) * mm, "end": v(35.72, 17.33) * mm});
            skLineSegment(sketch, "E365", {"start": v(35.72, 17.33) * mm, "end": v(35.85, 17.24) * mm});
            skLineSegment(sketch, "E366", {"start": v(35.85, 17.24) * mm, "end": v(35.97, 17.15) * mm});
            skLineSegment(sketch, "E367", {"start": v(35.97, 17.15) * mm, "end": v(36.1, 17.04) * mm});
            skLineSegment(sketch, "E368", {"start": v(36.1, 17.04) * mm, "end": v(36.2, 16.92) * mm});
            skLineSegment(sketch, "E369", {"start": v(36.2, 16.92) * mm, "end": v(36.3, 16.8) * mm});
            skLineSegment(sketch, "E370", {"start": v(36.3, 16.8) * mm, "end": v(36.38, 16.67) * mm});
            skLineSegment(sketch, "E371", {"start": v(36.38, 16.67) * mm, "end": v(36.46, 16.53) * mm});
            skLineSegment(sketch, "E372", {"start": v(36.46, 16.53) * mm, "end": v(36.52, 16.4) * mm});
            skLineSegment(sketch, "E373", {"start": v(36.52, 16.4) * mm, "end": v(36.58, 16.24) * mm});
            skLineSegment(sketch, "E374", {"start": v(36.58, 16.24) * mm, "end": v(36.62, 16.1) * mm});
            skLineSegment(sketch, "E375", {"start": v(36.62, 16.1) * mm, "end": v(36.65, 15.94) * mm});
            skLineSegment(sketch, "E376", {"start": v(36.65, 15.94) * mm, "end": v(36.67, 15.78) * mm});
            skLineSegment(sketch, "E377", {"start": v(36.67, 15.78) * mm, "end": v(36.68, 15.62) * mm});
            skLineSegment(sketch, "E378", {"start": v(36.68, 15.62) * mm, "end": v(36.68, -15.63) * mm});
            skLineSegment(sketch, "E379", {"start": v(36.68, -15.63) * mm, "end": v(36.67, -15.78) * mm});
            skLineSegment(sketch, "E380", {"start": v(36.67, -15.78) * mm, "end": v(36.65, -15.94) * mm});
            skLineSegment(sketch, "E381", {"start": v(36.65, -15.94) * mm, "end": v(36.62, -16.1) * mm});
            skLineSegment(sketch, "E382", {"start": v(36.62, -16.1) * mm, "end": v(36.58, -16.24) * mm});
            skLineSegment(sketch, "E383", {"start": v(36.58, -16.24) * mm, "end": v(36.52, -16.4) * mm});
            skLineSegment(sketch, "E384", {"start": v(36.52, -16.4) * mm, "end": v(36.46, -16.53) * mm});
            skLineSegment(sketch, "E385", {"start": v(36.46, -16.53) * mm, "end": v(36.38, -16.67) * mm});
            skLineSegment(sketch, "E386", {"start": v(36.38, -16.67) * mm, "end": v(36.3, -16.8) * mm});
            skLineSegment(sketch, "E387", {"start": v(36.3, -16.8) * mm, "end": v(36.2, -16.92) * mm});
            skLineSegment(sketch, "E388", {"start": v(36.2, -16.92) * mm, "end": v(36.1, -17.04) * mm});
            skLineSegment(sketch, "E389", {"start": v(36.1, -17.04) * mm, "end": v(35.97, -17.15) * mm});
            skLineSegment(sketch, "E390", {"start": v(35.97, -17.15) * mm, "end": v(35.85, -17.24) * mm});
            skLineSegment(sketch, "E391", {"start": v(35.85, -17.24) * mm, "end": v(35.72, -17.33) * mm});
            skLineSegment(sketch, "E392", {"start": v(35.72, -17.33) * mm, "end": v(35.58, -17.4) * mm});
            skLineSegment(sketch, "E393", {"start": v(35.58, -17.4) * mm, "end": v(35.44, -17.47) * mm});
            skLineSegment(sketch, "E394", {"start": v(35.44, -17.47) * mm, "end": v(35.3, -17.53) * mm});
            skLineSegment(sketch, "E395", {"start": v(35.3, -17.53) * mm, "end": v(35.14, -17.57) * mm});
            skLineSegment(sketch, "E396", {"start": v(35.14, -17.57) * mm, "end": v(34.99, -17.6) * mm});
            skLineSegment(sketch, "E397", {"start": v(34.99, -17.6) * mm, "end": v(34.83, -17.62) * mm});
            skLineSegment(sketch, "E398", {"start": v(34.83, -17.62) * mm, "end": v(34.68, -17.63) * mm});
            skLineSegment(sketch, "E399", {"start": v(34.68, -17.63) * mm, "end": v(-34.67, -17.63) * mm});
            skLineSegment(sketch, "E400", {"start": v(-34.67, -17.63) * mm, "end": v(-34.83, -17.62) * mm});
            skLineSegment(sketch, "E401", {"start": v(-34.83, -17.62) * mm, "end": v(-34.99, -17.6) * mm});
            skLineSegment(sketch, "E402", {"start": v(-34.99, -17.6) * mm, "end": v(-35.14, -17.57) * mm});
            skLineSegment(sketch, "E403", {"start": v(-35.14, -17.57) * mm, "end": v(-35.3, -17.53) * mm});
            skLineSegment(sketch, "E404", {"start": v(-35.3, -17.53) * mm, "end": v(-35.44, -17.47) * mm});
            skLineSegment(sketch, "E405", {"start": v(-35.44, -17.47) * mm, "end": v(-35.58, -17.4) * mm});
            skLineSegment(sketch, "E406", {"start": v(-35.58, -17.4) * mm, "end": v(-35.72, -17.33) * mm});
            skLineSegment(sketch, "E407", {"start": v(-35.72, -17.33) * mm, "end": v(-35.85, -17.24) * mm});
            skLineSegment(sketch, "E408", {"start": v(-35.85, -17.24) * mm, "end": v(-35.97, -17.15) * mm});
            skLineSegment(sketch, "E409", {"start": v(-35.97, -17.15) * mm, "end": v(-36.1, -17.04) * mm});
            skLineSegment(sketch, "E410", {"start": v(-36.1, -17.04) * mm, "end": v(-36.2, -16.92) * mm});
            skLineSegment(sketch, "E411", {"start": v(-36.2, -16.92) * mm, "end": v(-36.3, -16.8) * mm});
            skLineSegment(sketch, "E412", {"start": v(-36.3, -16.8) * mm, "end": v(-36.38, -16.67) * mm});
            skLineSegment(sketch, "E413", {"start": v(-36.38, -16.67) * mm, "end": v(-36.46, -16.53) * mm});
            skLineSegment(sketch, "E414", {"start": v(-36.46, -16.53) * mm, "end": v(-36.52, -16.4) * mm});
            skLineSegment(sketch, "E415", {"start": v(-36.52, -16.4) * mm, "end": v(-36.58, -16.24) * mm});
            skLineSegment(sketch, "E416", {"start": v(-36.58, -16.24) * mm, "end": v(-36.62, -16.1) * mm});
            skLineSegment(sketch, "E417", {"start": v(-36.62, -16.1) * mm, "end": v(-36.65, -15.94) * mm});
            skLineSegment(sketch, "E418", {"start": v(-36.65, -15.94) * mm, "end": v(-36.67, -15.78) * mm});
            skLineSegment(sketch, "E419", {"start": v(-36.67, -15.78) * mm, "end": v(-36.68, -15.62) * mm});
            skLineSegment(sketch, "E420", {"start": v(-36.68, -15.62) * mm, "end": v(-36.67, 15.62) * mm});
            skLineSegment(sketch, "E421", {"start": v(-36.67, 15.62) * mm, "end": v(-36.67, 15.78) * mm});
            skLineSegment(sketch, "E422", {"start": v(-36.67, 15.78) * mm, "end": v(-36.65, 15.94) * mm});
            skLineSegment(sketch, "E423", {"start": v(-36.65, 15.94) * mm, "end": v(-36.62, 16.1) * mm});
            skLineSegment(sketch, "E424", {"start": v(-36.62, 16.1) * mm, "end": v(-36.58, 16.24) * mm});
            skLineSegment(sketch, "E425", {"start": v(-36.58, 16.24) * mm, "end": v(-36.52, 16.4) * mm});
            skLineSegment(sketch, "E426", {"start": v(-36.52, 16.4) * mm, "end": v(-36.46, 16.53) * mm});
            skLineSegment(sketch, "E427", {"start": v(-36.46, 16.53) * mm, "end": v(-36.38, 16.67) * mm});
            skLineSegment(sketch, "E428", {"start": v(-36.38, 16.67) * mm, "end": v(-36.3, 16.8) * mm});
            skLineSegment(sketch, "E429", {"start": v(-36.3, 16.8) * mm, "end": v(-36.2, 16.92) * mm});
            skLineSegment(sketch, "E430", {"start": v(-36.2, 16.92) * mm, "end": v(-36.1, 17.04) * mm});
            skLineSegment(sketch, "E431", {"start": v(-36.1, 17.04) * mm, "end": v(-35.97, 17.15) * mm});
            skLineSegment(sketch, "E432", {"start": v(-35.97, 17.15) * mm, "end": v(-35.85, 17.24) * mm});
            skLineSegment(sketch, "E433", {"start": v(-35.85, 17.24) * mm, "end": v(-35.72, 17.33) * mm});
            skLineSegment(sketch, "E434", {"start": v(-35.72, 17.33) * mm, "end": v(-35.58, 17.4) * mm});
            skLineSegment(sketch, "E435", {"start": v(-35.58, 17.4) * mm, "end": v(-35.44, 17.47) * mm});
            skLineSegment(sketch, "E436", {"start": v(-35.44, 17.47) * mm, "end": v(-35.3, 17.53) * mm});
            skLineSegment(sketch, "E437", {"start": v(-35.3, 17.53) * mm, "end": v(-35.14, 17.57) * mm});
            skLineSegment(sketch, "E438", {"start": v(-35.14, 17.57) * mm, "end": v(-34.99, 17.6) * mm});
            skLineSegment(sketch, "E439", {"start": v(-34.99, 17.6) * mm, "end": v(-34.83, 17.62) * mm});
            skLineSegment(sketch, "E440", {"start": v(-34.83, 17.62) * mm, "end": v(-34.67, 17.63) * mm});
            skLineSegment(sketch, "E441", {"start": v(-34.67, 17.63) * mm, "end": v(34.68, 17.62) * mm});
            skLineSegment(sketch, "E442", {"start": v(33.14, -13.2) * mm, "end": v(32.75, -13.4) * mm});
            skLineSegment(sketch, "E443", {"start": v(32.75, -13.4) * mm, "end": v(32.44, -13.7) * mm});
            skLineSegment(sketch, "E444", {"start": v(32.44, -13.7) * mm, "end": v(32.24, -14.1) * mm});
            skLineSegment(sketch, "E445", {"start": v(32.24, -14.1) * mm, "end": v(32.18, -14.53) * mm});
            skLineSegment(sketch, "E446", {"start": v(32.18, -14.53) * mm, "end": v(32.24, -14.96) * mm});
            skLineSegment(sketch, "E447", {"start": v(32.24, -14.96) * mm, "end": v(32.44, -15.35) * mm});
            skLineSegment(sketch, "E448", {"start": v(32.44, -15.35) * mm, "end": v(32.75, -15.66) * mm});
            skLineSegment(sketch, "E449", {"start": v(32.75, -15.66) * mm, "end": v(33.14, -15.86) * mm});
            skLineSegment(sketch, "E450", {"start": v(33.14, -15.86) * mm, "end": v(33.58, -15.93) * mm});
            skLineSegment(sketch, "E451", {"start": v(33.58, -15.93) * mm, "end": v(34, -15.86) * mm});
            skLineSegment(sketch, "E452", {"start": v(34, -15.86) * mm, "end": v(34.4, -15.66) * mm});
            skLineSegment(sketch, "E453", {"start": v(34.4, -15.66) * mm, "end": v(34.7, -15.35) * mm});
            skLineSegment(sketch, "E454", {"start": v(34.7, -15.35) * mm, "end": v(34.9, -14.96) * mm});
            skLineSegment(sketch, "E455", {"start": v(34.9, -14.96) * mm, "end": v(34.98, -14.53) * mm});
            skLineSegment(sketch, "E456", {"start": v(34.98, -14.53) * mm, "end": v(34.9, -14.1) * mm});
            skLineSegment(sketch, "E457", {"start": v(34.9, -14.1) * mm, "end": v(34.7, -13.7) * mm});
            skLineSegment(sketch, "E458", {"start": v(34.7, -13.7) * mm, "end": v(34.4, -13.4) * mm});
            skLineSegment(sketch, "E459", {"start": v(34.4, -13.4) * mm, "end": v(34, -13.2) * mm});
            skLineSegment(sketch, "E460", {"start": v(34, -13.2) * mm, "end": v(33.58, -13.13) * mm});
            skLineSegment(sketch, "E461", {"start": v(33.58, -13.13) * mm, "end": v(33.14, -13.2) * mm});
            skLineSegment(sketch, "E462", {"start": v(-34, -13.2) * mm, "end": v(-34.4, -13.4) * mm});
            skLineSegment(sketch, "E463", {"start": v(-34.4, -13.4) * mm, "end": v(-34.7, -13.7) * mm});
            skLineSegment(sketch, "E464", {"start": v(-34.7, -13.7) * mm, "end": v(-34.9, -14.1) * mm});
            skLineSegment(sketch, "E465", {"start": v(-34.9, -14.1) * mm, "end": v(-34.98, -14.53) * mm});
            skLineSegment(sketch, "E466", {"start": v(-34.98, -14.53) * mm, "end": v(-34.9, -14.96) * mm});
            skLineSegment(sketch, "E467", {"start": v(-34.9, -14.96) * mm, "end": v(-34.7, -15.35) * mm});
            skLineSegment(sketch, "E468", {"start": v(-34.7, -15.35) * mm, "end": v(-34.4, -15.66) * mm});
            skLineSegment(sketch, "E469", {"start": v(-34.4, -15.66) * mm, "end": v(-34, -15.86) * mm});
            skLineSegment(sketch, "E470", {"start": v(-34, -15.86) * mm, "end": v(-33.58, -15.93) * mm});
            skLineSegment(sketch, "E471", {"start": v(-33.58, -15.93) * mm, "end": v(-33.14, -15.86) * mm});
            skLineSegment(sketch, "E472", {"start": v(-33.14, -15.86) * mm, "end": v(-32.75, -15.66) * mm});
            skLineSegment(sketch, "E473", {"start": v(-32.75, -15.66) * mm, "end": v(-32.44, -15.35) * mm});
            skLineSegment(sketch, "E474", {"start": v(-32.44, -15.35) * mm, "end": v(-32.24, -14.96) * mm});
            skLineSegment(sketch, "E475", {"start": v(-32.24, -14.96) * mm, "end": v(-32.18, -14.53) * mm});
            skLineSegment(sketch, "E476", {"start": v(-32.18, -14.53) * mm, "end": v(-32.24, -14.1) * mm});
            skLineSegment(sketch, "E477", {"start": v(-32.24, -14.1) * mm, "end": v(-32.44, -13.7) * mm});
            skLineSegment(sketch, "E478", {"start": v(-32.44, -13.7) * mm, "end": v(-32.75, -13.4) * mm});
            skLineSegment(sketch, "E479", {"start": v(-32.75, -13.4) * mm, "end": v(-33.14, -13.2) * mm});
            skLineSegment(sketch, "E480", {"start": v(-33.14, -13.2) * mm, "end": v(-33.58, -13.13) * mm});
            skLineSegment(sketch, "E481", {"start": v(-33.58, -13.13) * mm, "end": v(-34, -13.2) * mm});
            skLineSegment(sketch, "E482", {"start": v(-25.95, 6.9) * mm, "end": v(-25.95, 5.9) * mm});
            skLineSegment(sketch, "E483", {"start": v(-25.95, 5.9) * mm, "end": v(-26.75, 5.9) * mm});
            skLineSegment(sketch, "E484", {"start": v(-26.75, 5.9) * mm, "end": v(-26.75, 3) * mm});
            skLineSegment(sketch, "E485", {"start": v(-26.75, 3) * mm, "end": v(-25.95, 3) * mm});
            skLineSegment(sketch, "E486", {"start": v(-25.95, 3) * mm, "end": v(-25.95, -3) * mm});
            skLineSegment(sketch, "E487", {"start": v(-25.95, -3) * mm, "end": v(-26.75, -3) * mm});
            skLineSegment(sketch, "E488", {"start": v(-26.75, -3) * mm, "end": v(-26.75, -5.9) * mm});
            skLineSegment(sketch, "E489", {"start": v(-26.75, -5.9) * mm, "end": v(-25.95, -5.9) * mm});
            skLineSegment(sketch, "E490", {"start": v(-25.95, -5.9) * mm, "end": v(-25.95, -6.9) * mm});
            skLineSegment(sketch, "E491", {"start": v(-25.95, -6.9) * mm, "end": v(-12.15, -6.9) * mm});
            skLineSegment(sketch, "E492", {"start": v(-12.15, -6.9) * mm, "end": v(-12.15, -5.9) * mm});
            skLineSegment(sketch, "E493", {"start": v(-12.15, -5.9) * mm, "end": v(-11.35, -5.9) * mm});
            skLineSegment(sketch, "E494", {"start": v(-11.35, -5.9) * mm, "end": v(-11.35, -3) * mm});
            skLineSegment(sketch, "E495", {"start": v(-11.35, -3) * mm, "end": v(-12.15, -3) * mm});
            skLineSegment(sketch, "E496", {"start": v(-12.15, -3) * mm, "end": v(-12.15, 3) * mm});
            skLineSegment(sketch, "E497", {"start": v(-12.15, 3) * mm, "end": v(-11.35, 3) * mm});
            skLineSegment(sketch, "E498", {"start": v(-11.35, 3) * mm, "end": v(-11.35, 5.9) * mm});
            skLineSegment(sketch, "E499", {"start": v(-11.35, 5.9) * mm, "end": v(-12.15, 5.9) * mm});
            skLineSegment(sketch, "E500", {"start": v(-12.15, 5.9) * mm, "end": v(-12.15, 6.9) * mm});
            skLineSegment(sketch, "E501", {"start": v(-12.15, 6.9) * mm, "end": v(-25.95, 6.9) * mm});
            skLineSegment(sketch, "E502", {"start": v(-6.9, 6.9) * mm, "end": v(-6.9, 5.9) * mm});
            skLineSegment(sketch, "E503", {"start": v(-6.9, 5.9) * mm, "end": v(-7.7, 5.9) * mm});
            skLineSegment(sketch, "E504", {"start": v(-7.7, 5.9) * mm, "end": v(-7.7, 3) * mm});
            skLineSegment(sketch, "E505", {"start": v(-7.7, 3) * mm, "end": v(-6.9, 3) * mm});
            skLineSegment(sketch, "E506", {"start": v(-6.9, 3) * mm, "end": v(-6.9, -3) * mm});
            skLineSegment(sketch, "E507", {"start": v(-6.9, -3) * mm, "end": v(-7.7, -3) * mm});
            skLineSegment(sketch, "E508", {"start": v(-7.7, -3) * mm, "end": v(-7.7, -5.9) * mm});
            skLineSegment(sketch, "E509", {"start": v(-7.7, -5.9) * mm, "end": v(-6.9, -5.9) * mm});
            skLineSegment(sketch, "E510", {"start": v(-6.9, -5.9) * mm, "end": v(-6.9, -6.9) * mm});
            skLineSegment(sketch, "E511", {"start": v(-6.9, -6.9) * mm, "end": v(6.9, -6.9) * mm});
            skLineSegment(sketch, "E512", {"start": v(6.9, -6.9) * mm, "end": v(6.9, -5.9) * mm});
            skLineSegment(sketch, "E513", {"start": v(6.9, -5.9) * mm, "end": v(7.7, -5.9) * mm});
            skLineSegment(sketch, "E514", {"start": v(7.7, -5.9) * mm, "end": v(7.7, -3) * mm});
            skLineSegment(sketch, "E515", {"start": v(7.7, -3) * mm, "end": v(6.9, -3) * mm});
            skLineSegment(sketch, "E516", {"start": v(6.9, -3) * mm, "end": v(6.9, 3) * mm});
            skLineSegment(sketch, "E517", {"start": v(6.9, 3) * mm, "end": v(7.7, 3) * mm});
            skLineSegment(sketch, "E518", {"start": v(7.7, 3) * mm, "end": v(7.7, 5.9) * mm});
            skLineSegment(sketch, "E519", {"start": v(7.7, 5.9) * mm, "end": v(6.9, 5.9) * mm});
            skLineSegment(sketch, "E520", {"start": v(6.9, 5.9) * mm, "end": v(6.9, 6.9) * mm});
            skLineSegment(sketch, "E521", {"start": v(6.9, 6.9) * mm, "end": v(-6.9, 6.9) * mm});
            skLineSegment(sketch, "E522", {"start": v(12.15, 6.9) * mm, "end": v(12.15, 5.9) * mm});
            skLineSegment(sketch, "E523", {"start": v(12.15, 5.9) * mm, "end": v(11.35, 5.9) * mm});
            skLineSegment(sketch, "E524", {"start": v(11.35, 5.9) * mm, "end": v(11.35, 3) * mm});
            skLineSegment(sketch, "E525", {"start": v(11.35, 3) * mm, "end": v(12.15, 3) * mm});
            skLineSegment(sketch, "E526", {"start": v(12.15, 3) * mm, "end": v(12.15, -3) * mm});
            skLineSegment(sketch, "E527", {"start": v(12.15, -3) * mm, "end": v(11.35, -3) * mm});
            skLineSegment(sketch, "E528", {"start": v(11.35, -3) * mm, "end": v(11.35, -5.9) * mm});
            skLineSegment(sketch, "E529", {"start": v(11.35, -5.9) * mm, "end": v(12.15, -5.9) * mm});
            skLineSegment(sketch, "E530", {"start": v(12.15, -5.9) * mm, "end": v(12.15, -6.9) * mm});
            skLineSegment(sketch, "E531", {"start": v(12.15, -6.9) * mm, "end": v(25.95, -6.9) * mm});
            skLineSegment(sketch, "E532", {"start": v(25.95, -6.9) * mm, "end": v(25.95, -5.9) * mm});
            skLineSegment(sketch, "E533", {"start": v(25.95, -5.9) * mm, "end": v(26.75, -5.9) * mm});
            skLineSegment(sketch, "E534", {"start": v(26.75, -5.9) * mm, "end": v(26.75, -3) * mm});
            skLineSegment(sketch, "E535", {"start": v(26.75, -3) * mm, "end": v(25.95, -3) * mm});
            skLineSegment(sketch, "E536", {"start": v(25.95, -3) * mm, "end": v(25.95, 3) * mm});
            skLineSegment(sketch, "E537", {"start": v(25.95, 3) * mm, "end": v(26.75, 3) * mm});
            skLineSegment(sketch, "E538", {"start": v(26.75, 3) * mm, "end": v(26.75, 5.9) * mm});
            skLineSegment(sketch, "E539", {"start": v(26.75, 5.9) * mm, "end": v(25.95, 5.9) * mm});
            skLineSegment(sketch, "E540", {"start": v(25.95, 5.9) * mm, "end": v(25.95, 6.9) * mm});
            skLineSegment(sketch, "E541", {"start": v(25.95, 6.9) * mm, "end": v(12.15, 6.9) * mm});
            skLineSegment(sketch, "E542", {"start": v(33.14, 15.86) * mm, "end": v(32.75, 15.66) * mm});
            skLineSegment(sketch, "E543", {"start": v(32.75, 15.66) * mm, "end": v(32.44, 15.35) * mm});
            skLineSegment(sketch, "E544", {"start": v(32.44, 15.35) * mm, "end": v(32.24, 14.96) * mm});
            skLineSegment(sketch, "E545", {"start": v(32.24, 14.96) * mm, "end": v(32.18, 14.53) * mm});
            skLineSegment(sketch, "E546", {"start": v(32.18, 14.53) * mm, "end": v(32.24, 14.1) * mm});
            skLineSegment(sketch, "E547", {"start": v(32.24, 14.1) * mm, "end": v(32.44, 13.7) * mm});
            skLineSegment(sketch, "E548", {"start": v(32.44, 13.7) * mm, "end": v(32.75, 13.4) * mm});
            skLineSegment(sketch, "E549", {"start": v(32.75, 13.4) * mm, "end": v(33.14, 13.2) * mm});
            skLineSegment(sketch, "E550", {"start": v(33.14, 13.2) * mm, "end": v(33.58, 13.13) * mm});
            skLineSegment(sketch, "E551", {"start": v(33.58, 13.13) * mm, "end": v(34, 13.2) * mm});
            skLineSegment(sketch, "E552", {"start": v(34, 13.2) * mm, "end": v(34.4, 13.4) * mm});
            skLineSegment(sketch, "E553", {"start": v(34.4, 13.4) * mm, "end": v(34.7, 13.7) * mm});
            skLineSegment(sketch, "E554", {"start": v(34.7, 13.7) * mm, "end": v(34.9, 14.1) * mm});
            skLineSegment(sketch, "E555", {"start": v(34.9, 14.1) * mm, "end": v(34.98, 14.53) * mm});
            skLineSegment(sketch, "E556", {"start": v(34.98, 14.53) * mm, "end": v(34.9, 14.96) * mm});
            skLineSegment(sketch, "E557", {"start": v(34.9, 14.96) * mm, "end": v(34.7, 15.35) * mm});
            skLineSegment(sketch, "E558", {"start": v(34.7, 15.35) * mm, "end": v(34.4, 15.66) * mm});
            skLineSegment(sketch, "E559", {"start": v(34.4, 15.66) * mm, "end": v(34, 15.86) * mm});
            skLineSegment(sketch, "E560", {"start": v(34, 15.86) * mm, "end": v(33.58, 15.93) * mm});
            skLineSegment(sketch, "E561", {"start": v(33.58, 15.93) * mm, "end": v(33.14, 15.86) * mm});
            skLineSegment(sketch, "E562", {"start": v(-34, 15.86) * mm, "end": v(-34.4, 15.66) * mm});
            skLineSegment(sketch, "E563", {"start": v(-34.4, 15.66) * mm, "end": v(-34.7, 15.35) * mm});
            skLineSegment(sketch, "E564", {"start": v(-34.7, 15.35) * mm, "end": v(-34.9, 14.96) * mm});
            skLineSegment(sketch, "E565", {"start": v(-34.9, 14.96) * mm, "end": v(-34.98, 14.53) * mm});
            skLineSegment(sketch, "E566", {"start": v(-34.98, 14.53) * mm, "end": v(-34.9, 14.1) * mm});
            skLineSegment(sketch, "E567", {"start": v(-34.9, 14.1) * mm, "end": v(-34.7, 13.7) * mm});
            skLineSegment(sketch, "E568", {"start": v(-34.7, 13.7) * mm, "end": v(-34.4, 13.4) * mm});
            skLineSegment(sketch, "E569", {"start": v(-34.4, 13.4) * mm, "end": v(-34, 13.2) * mm});
            skLineSegment(sketch, "E570", {"start": v(-34, 13.2) * mm, "end": v(-33.58, 13.13) * mm});
            skLineSegment(sketch, "E571", {"start": v(-33.58, 13.13) * mm, "end": v(-33.14, 13.2) * mm});
            skLineSegment(sketch, "E572", {"start": v(-33.14, 13.2) * mm, "end": v(-32.75, 13.4) * mm});
            skLineSegment(sketch, "E573", {"start": v(-32.75, 13.4) * mm, "end": v(-32.44, 13.7) * mm});
            skLineSegment(sketch, "E574", {"start": v(-32.44, 13.7) * mm, "end": v(-32.24, 14.1) * mm});
            skLineSegment(sketch, "E575", {"start": v(-32.24, 14.1) * mm, "end": v(-32.18, 14.53) * mm});
            skLineSegment(sketch, "E576", {"start": v(-32.18, 14.53) * mm, "end": v(-32.24, 14.96) * mm});
            skLineSegment(sketch, "E577", {"start": v(-32.24, 14.96) * mm, "end": v(-32.44, 15.35) * mm});
            skLineSegment(sketch, "E578", {"start": v(-32.44, 15.35) * mm, "end": v(-32.75, 15.66) * mm});
            skLineSegment(sketch, "E579", {"start": v(-32.75, 15.66) * mm, "end": v(-33.14, 15.86) * mm});
            skLineSegment(sketch, "E580", {"start": v(-33.14, 15.86) * mm, "end": v(-33.58, 15.93) * mm});
            skLineSegment(sketch, "E581", {"start": v(-33.58, 15.93) * mm, "end": v(-34, 15.86) * mm});
            skSolve(sketch);
        }
        {
            var Q0;
            Q0 = qSketchRegion(id + "F7", true);
            extrude(context, id + "F8", {"entities" : qUnion([Q0]), "depth" : (getVariable(context, 'Thickness') / 2) * mm, "offsetDistance" : 25 * mm});
        }
        {
            var Q0;
            Q0=makeQuery(id+"F8.opExtrude","CAP_FACE",FACE,{"disambiguationData":[OSD([sQuery(id+"F7.wireOp",EDGE,"E358"),sQuery(id+"F7.wireOp",EDGE,"E359"),sQuery(id+"F7.wireOp",EDGE,"E360"),sQuery(id+"F7.wireOp",EDGE,"E361"),sQuery(id+"F7.wireOp",EDGE,"E362"),sQuery(id+"F7.wireOp",EDGE,"E363"),sQuery(id+"F7.wireOp",EDGE,"E364"),sQuery(id+"F7.wireOp",EDGE,"E365"),sQuery(id+"F7.wireOp",EDGE,"E366"),sQuery(id+"F7.wireOp",EDGE,"E367"),sQuery(id+"F7.wireOp",EDGE,"E368"),sQuery(id+"F7.wireOp",EDGE,"E369"),sQuery(id+"F7.wireOp",EDGE,"E370"),sQuery(id+"F7.wireOp",EDGE,"E371"),sQuery(id+"F7.wireOp",EDGE,"E372"),sQuery(id+"F7.wireOp",EDGE,"E373"),sQuery(id+"F7.wireOp",EDGE,"E374"),sQuery(id+"F7.wireOp",EDGE,"E375"),sQuery(id+"F7.wireOp",EDGE,"E376"),sQuery(id+"F7.wireOp",EDGE,"E377"),sQuery(id+"F7.wireOp",EDGE,"E378"),sQuery(id+"F7.wireOp",EDGE,"E379"),sQuery(id+"F7.wireOp",EDGE,"E380"),sQuery(id+"F7.wireOp",EDGE,"E381"),sQuery(id+"F7.wireOp",EDGE,"E382"),sQuery(id+"F7.wireOp",EDGE,"E383"),sQuery(id+"F7.wireOp",EDGE,"E384"),sQuery(id+"F7.wireOp",EDGE,"E385"),sQuery(id+"F7.wireOp",EDGE,"E386"),sQuery(id+"F7.wireOp",EDGE,"E387"),sQuery(id+"F7.wireOp",EDGE,"E388"),sQuery(id+"F7.wireOp",EDGE,"E389"),sQuery(id+"F7.wireOp",EDGE,"E390"),sQuery(id+"F7.wireOp",EDGE,"E391"),sQuery(id+"F7.wireOp",EDGE,"E392"),sQuery(id+"F7.wireOp",EDGE,"E393"),sQuery(id+"F7.wireOp",EDGE,"E394"),sQuery(id+"F7.wireOp",EDGE,"E395"),sQuery(id+"F7.wireOp",EDGE,"E396"),sQuery(id+"F7.wireOp",EDGE,"E397"),sQuery(id+"F7.wireOp",EDGE,"E398"),sQuery(id+"F7.wireOp",EDGE,"E399"),sQuery(id+"F7.wireOp",EDGE,"E400"),sQuery(id+"F7.wireOp",EDGE,"E401"),sQuery(id+"F7.wireOp",EDGE,"E402"),sQuery(id+"F7.wireOp",EDGE,"E403"),sQuery(id+"F7.wireOp",EDGE,"E404"),sQuery(id+"F7.wireOp",EDGE,"E405"),sQuery(id+"F7.wireOp",EDGE,"E406"),sQuery(id+"F7.wireOp",EDGE,"E407"),sQuery(id+"F7.wireOp",EDGE,"E408"),sQuery(id+"F7.wireOp",EDGE,"E409"),sQuery(id+"F7.wireOp",EDGE,"E410"),sQuery(id+"F7.wireOp",EDGE,"E411"),sQuery(id+"F7.wireOp",EDGE,"E412"),sQuery(id+"F7.wireOp",EDGE,"E413"),sQuery(id+"F7.wireOp",EDGE,"E414"),sQuery(id+"F7.wireOp",EDGE,"E415"),sQuery(id+"F7.wireOp",EDGE,"E416"),sQuery(id+"F7.wireOp",EDGE,"E417"),sQuery(id+"F7.wireOp",EDGE,"E418"),sQuery(id+"F7.wireOp",EDGE,"E419"),sQuery(id+"F7.wireOp",EDGE,"E420"),sQuery(id+"F7.wireOp",EDGE,"E421"),sQuery(id+"F7.wireOp",EDGE,"E422"),sQuery(id+"F7.wireOp",EDGE,"E423"),sQuery(id+"F7.wireOp",EDGE,"E424"),sQuery(id+"F7.wireOp",EDGE,"E425"),sQuery(id+"F7.wireOp",EDGE,"E426"),sQuery(id+"F7.wireOp",EDGE,"E427"),sQuery(id+"F7.wireOp",EDGE,"E428"),sQuery(id+"F7.wireOp",EDGE,"E429"),sQuery(id+"F7.wireOp",EDGE,"E430"),sQuery(id+"F7.wireOp",EDGE,"E431"),sQuery(id+"F7.wireOp",EDGE,"E432"),sQuery(id+"F7.wireOp",EDGE,"E433"),sQuery(id+"F7.wireOp",EDGE,"E434"),sQuery(id+"F7.wireOp",EDGE,"E435"),sQuery(id+"F7.wireOp",EDGE,"E436"),sQuery(id+"F7.wireOp",EDGE,"E437"),sQuery(id+"F7.wireOp",EDGE,"E438"),sQuery(id+"F7.wireOp",EDGE,"E439"),sQuery(id+"F7.wireOp",EDGE,"E440"),sQuery(id+"F7.wireOp",EDGE,"E441"),sQuery(id+"F7.wireOp",EDGE,"E442"),sQuery(id+"F7.wireOp",EDGE,"E443"),sQuery(id+"F7.wireOp",EDGE,"E444"),sQuery(id+"F7.wireOp",EDGE,"E445"),sQuery(id+"F7.wireOp",EDGE,"E446"),sQuery(id+"F7.wireOp",EDGE,"E447"),sQuery(id+"F7.wireOp",EDGE,"E448"),sQuery(id+"F7.wireOp",EDGE,"E449"),sQuery(id+"F7.wireOp",EDGE,"E450"),sQuery(id+"F7.wireOp",EDGE,"E451"),sQuery(id+"F7.wireOp",EDGE,"E452"),sQuery(id+"F7.wireOp",EDGE,"E453"),sQuery(id+"F7.wireOp",EDGE,"E454"),sQuery(id+"F7.wireOp",EDGE,"E455"),sQuery(id+"F7.wireOp",EDGE,"E456"),sQuery(id+"F7.wireOp",EDGE,"E457"),sQuery(id+"F7.wireOp",EDGE,"E458"),sQuery(id+"F7.wireOp",EDGE,"E459"),sQuery(id+"F7.wireOp",EDGE,"E460"),sQuery(id+"F7.wireOp",EDGE,"E461"),sQuery(id+"F7.wireOp",EDGE,"E462"),sQuery(id+"F7.wireOp",EDGE,"E463"),sQuery(id+"F7.wireOp",EDGE,"E464"),sQuery(id+"F7.wireOp",EDGE,"E465"),sQuery(id+"F7.wireOp",EDGE,"E466"),sQuery(id+"F7.wireOp",EDGE,"E467"),sQuery(id+"F7.wireOp",EDGE,"E468"),sQuery(id+"F7.wireOp",EDGE,"E469"),sQuery(id+"F7.wireOp",EDGE,"E470"),sQuery(id+"F7.wireOp",EDGE,"E471"),sQuery(id+"F7.wireOp",EDGE,"E472"),sQuery(id+"F7.wireOp",EDGE,"E473"),sQuery(id+"F7.wireOp",EDGE,"E474"),sQuery(id+"F7.wireOp",EDGE,"E475"),sQuery(id+"F7.wireOp",EDGE,"E476"),sQuery(id+"F7.wireOp",EDGE,"E477"),sQuery(id+"F7.wireOp",EDGE,"E478"),sQuery(id+"F7.wireOp",EDGE,"E479"),sQuery(id+"F7.wireOp",EDGE,"E480"),sQuery(id+"F7.wireOp",EDGE,"E481"),sQuery(id+"F7.wireOp",EDGE,"E482"),sQuery(id+"F7.wireOp",EDGE,"E483"),sQuery(id+"F7.wireOp",EDGE,"E484"),sQuery(id+"F7.wireOp",EDGE,"E485"),sQuery(id+"F7.wireOp",EDGE,"E486"),sQuery(id+"F7.wireOp",EDGE,"E487"),sQuery(id+"F7.wireOp",EDGE,"E488"),sQuery(id+"F7.wireOp",EDGE,"E489"),sQuery(id+"F7.wireOp",EDGE,"E490"),sQuery(id+"F7.wireOp",EDGE,"E491"),sQuery(id+"F7.wireOp",EDGE,"E492"),sQuery(id+"F7.wireOp",EDGE,"E493"),sQuery(id+"F7.wireOp",EDGE,"E494"),sQuery(id+"F7.wireOp",EDGE,"E495"),sQuery(id+"F7.wireOp",EDGE,"E496"),sQuery(id+"F7.wireOp",EDGE,"E497"),sQuery(id+"F7.wireOp",EDGE,"E498"),sQuery(id+"F7.wireOp",EDGE,"E499"),sQuery(id+"F7.wireOp",EDGE,"E500"),sQuery(id+"F7.wireOp",EDGE,"E501"),sQuery(id+"F7.wireOp",EDGE,"E502"),sQuery(id+"F7.wireOp",EDGE,"E503"),sQuery(id+"F7.wireOp",EDGE,"E504"),sQuery(id+"F7.wireOp",EDGE,"E505"),sQuery(id+"F7.wireOp",EDGE,"E506"),sQuery(id+"F7.wireOp",EDGE,"E507"),sQuery(id+"F7.wireOp",EDGE,"E508"),sQuery(id+"F7.wireOp",EDGE,"E509"),sQuery(id+"F7.wireOp",EDGE,"E510"),sQuery(id+"F7.wireOp",EDGE,"E511"),sQuery(id+"F7.wireOp",EDGE,"E512"),sQuery(id+"F7.wireOp",EDGE,"E513"),sQuery(id+"F7.wireOp",EDGE,"E514"),sQuery(id+"F7.wireOp",EDGE,"E515"),sQuery(id+"F7.wireOp",EDGE,"E516"),sQuery(id+"F7.wireOp",EDGE,"E517"),sQuery(id+"F7.wireOp",EDGE,"E518"),sQuery(id+"F7.wireOp",EDGE,"E519"),sQuery(id+"F7.wireOp",EDGE,"E520"),sQuery(id+"F7.wireOp",EDGE,"E521"),sQuery(id+"F7.wireOp",EDGE,"E522"),sQuery(id+"F7.wireOp",EDGE,"E523"),sQuery(id+"F7.wireOp",EDGE,"E524"),sQuery(id+"F7.wireOp",EDGE,"E525"),sQuery(id+"F7.wireOp",EDGE,"E526"),sQuery(id+"F7.wireOp",EDGE,"E527"),sQuery(id+"F7.wireOp",EDGE,"E528"),sQuery(id+"F7.wireOp",EDGE,"E529"),sQuery(id+"F7.wireOp",EDGE,"E530"),sQuery(id+"F7.wireOp",EDGE,"E531"),sQuery(id+"F7.wireOp",EDGE,"E532"),sQuery(id+"F7.wireOp",EDGE,"E533"),sQuery(id+"F7.wireOp",EDGE,"E534"),sQuery(id+"F7.wireOp",EDGE,"E535"),sQuery(id+"F7.wireOp",EDGE,"E536"),sQuery(id+"F7.wireOp",EDGE,"E537"),sQuery(id+"F7.wireOp",EDGE,"E538"),sQuery(id+"F7.wireOp",EDGE,"E539"),sQuery(id+"F7.wireOp",EDGE,"E540"),sQuery(id+"F7.wireOp",EDGE,"E541"),sQuery(id+"F7.wireOp",EDGE,"E542"),sQuery(id+"F7.wireOp",EDGE,"E543"),sQuery(id+"F7.wireOp",EDGE,"E544"),sQuery(id+"F7.wireOp",EDGE,"E545"),sQuery(id+"F7.wireOp",EDGE,"E546"),sQuery(id+"F7.wireOp",EDGE,"E547"),sQuery(id+"F7.wireOp",EDGE,"E548"),sQuery(id+"F7.wireOp",EDGE,"E549"),sQuery(id+"F7.wireOp",EDGE,"E550"),sQuery(id+"F7.wireOp",EDGE,"E551"),sQuery(id+"F7.wireOp",EDGE,"E552"),sQuery(id+"F7.wireOp",EDGE,"E553"),sQuery(id+"F7.wireOp",EDGE,"E554"),sQuery(id+"F7.wireOp",EDGE,"E555"),sQuery(id+"F7.wireOp",EDGE,"E556"),sQuery(id+"F7.wireOp",EDGE,"E557"),sQuery(id+"F7.wireOp",EDGE,"E558"),sQuery(id+"F7.wireOp",EDGE,"E559"),sQuery(id+"F7.wireOp",EDGE,"E560"),sQuery(id+"F7.wireOp",EDGE,"E561"),sQuery(id+"F7.wireOp",EDGE,"E562"),sQuery(id+"F7.wireOp",EDGE,"E563"),sQuery(id+"F7.wireOp",EDGE,"E564"),sQuery(id+"F7.wireOp",EDGE,"E565"),sQuery(id+"F7.wireOp",EDGE,"E566"),sQuery(id+"F7.wireOp",EDGE,"E567"),sQuery(id+"F7.wireOp",EDGE,"E568"),sQuery(id+"F7.wireOp",EDGE,"E569"),sQuery(id+"F7.wireOp",EDGE,"E570"),sQuery(id+"F7.wireOp",EDGE,"E571"),sQuery(id+"F7.wireOp",EDGE,"E572"),sQuery(id+"F7.wireOp",EDGE,"E573"),sQuery(id+"F7.wireOp",EDGE,"E574"),sQuery(id+"F7.wireOp",EDGE,"E575"),sQuery(id+"F7.wireOp",EDGE,"E576"),sQuery(id+"F7.wireOp",EDGE,"E577"),sQuery(id+"F7.wireOp",EDGE,"E578"),sQuery(id+"F7.wireOp",EDGE,"E579"),sQuery(id+"F7.wireOp",EDGE,"E580"),sQuery(id+"F7.wireOp",EDGE,"E581")])],"isStart":false});
            var sketch = newSketch(context, id + "F9", { "sketchPlane" : qUnion([Q0])});
            skLineSegment(sketch, "E582", {"start": v(34.68, 17.62) * mm, "end": v(34.83, 17.62) * mm});
            skLineSegment(sketch, "E583", {"start": v(34.83, 17.62) * mm, "end": v(34.99, 17.6) * mm});
            skLineSegment(sketch, "E584", {"start": v(34.99, 17.6) * mm, "end": v(35.14, 17.57) * mm});
            skLineSegment(sketch, "E585", {"start": v(35.14, 17.57) * mm, "end": v(35.3, 17.53) * mm});
            skLineSegment(sketch, "E586", {"start": v(35.3, 17.53) * mm, "end": v(35.44, 17.47) * mm});
            skLineSegment(sketch, "E587", {"start": v(35.44, 17.47) * mm, "end": v(35.58, 17.4) * mm});
            skLineSegment(sketch, "E588", {"start": v(35.58, 17.4) * mm, "end": v(35.72, 17.33) * mm});
            skLineSegment(sketch, "E589", {"start": v(35.72, 17.33) * mm, "end": v(35.85, 17.24) * mm});
            skLineSegment(sketch, "E590", {"start": v(35.85, 17.24) * mm, "end": v(35.97, 17.15) * mm});
            skLineSegment(sketch, "E591", {"start": v(35.97, 17.15) * mm, "end": v(36.1, 17.04) * mm});
            skLineSegment(sketch, "E592", {"start": v(36.1, 17.04) * mm, "end": v(36.2, 16.92) * mm});
            skLineSegment(sketch, "E593", {"start": v(36.2, 16.92) * mm, "end": v(36.3, 16.8) * mm});
            skLineSegment(sketch, "E594", {"start": v(36.3, 16.8) * mm, "end": v(36.38, 16.67) * mm});
            skLineSegment(sketch, "E595", {"start": v(36.38, 16.67) * mm, "end": v(36.46, 16.53) * mm});
            skLineSegment(sketch, "E596", {"start": v(36.46, 16.53) * mm, "end": v(36.52, 16.4) * mm});
            skLineSegment(sketch, "E597", {"start": v(36.52, 16.4) * mm, "end": v(36.58, 16.24) * mm});
            skLineSegment(sketch, "E598", {"start": v(36.58, 16.24) * mm, "end": v(36.62, 16.1) * mm});
            skLineSegment(sketch, "E599", {"start": v(36.62, 16.1) * mm, "end": v(36.65, 15.94) * mm});
            skLineSegment(sketch, "E600", {"start": v(36.65, 15.94) * mm, "end": v(36.67, 15.78) * mm});
            skLineSegment(sketch, "E601", {"start": v(36.67, 15.78) * mm, "end": v(36.68, 15.62) * mm});
            skLineSegment(sketch, "E602", {"start": v(36.68, 15.62) * mm, "end": v(36.68, -15.63) * mm});
            skLineSegment(sketch, "E603", {"start": v(36.68, -15.63) * mm, "end": v(36.67, -15.78) * mm});
            skLineSegment(sketch, "E604", {"start": v(36.67, -15.78) * mm, "end": v(36.65, -15.94) * mm});
            skLineSegment(sketch, "E605", {"start": v(36.65, -15.94) * mm, "end": v(36.62, -16.1) * mm});
            skLineSegment(sketch, "E606", {"start": v(36.62, -16.1) * mm, "end": v(36.58, -16.24) * mm});
            skLineSegment(sketch, "E607", {"start": v(36.58, -16.24) * mm, "end": v(36.52, -16.4) * mm});
            skLineSegment(sketch, "E608", {"start": v(36.52, -16.4) * mm, "end": v(36.46, -16.53) * mm});
            skLineSegment(sketch, "E609", {"start": v(36.46, -16.53) * mm, "end": v(36.38, -16.67) * mm});
            skLineSegment(sketch, "E610", {"start": v(36.38, -16.67) * mm, "end": v(36.3, -16.8) * mm});
            skLineSegment(sketch, "E611", {"start": v(36.3, -16.8) * mm, "end": v(36.2, -16.92) * mm});
            skLineSegment(sketch, "E612", {"start": v(36.2, -16.92) * mm, "end": v(36.1, -17.04) * mm});
            skLineSegment(sketch, "E613", {"start": v(36.1, -17.04) * mm, "end": v(35.97, -17.15) * mm});
            skLineSegment(sketch, "E614", {"start": v(35.97, -17.15) * mm, "end": v(35.85, -17.24) * mm});
            skLineSegment(sketch, "E615", {"start": v(35.85, -17.24) * mm, "end": v(35.72, -17.33) * mm});
            skLineSegment(sketch, "E616", {"start": v(35.72, -17.33) * mm, "end": v(35.58, -17.4) * mm});
            skLineSegment(sketch, "E617", {"start": v(35.58, -17.4) * mm, "end": v(35.44, -17.47) * mm});
            skLineSegment(sketch, "E618", {"start": v(35.44, -17.47) * mm, "end": v(35.3, -17.53) * mm});
            skLineSegment(sketch, "E619", {"start": v(35.3, -17.53) * mm, "end": v(35.14, -17.57) * mm});
            skLineSegment(sketch, "E620", {"start": v(35.14, -17.57) * mm, "end": v(34.99, -17.6) * mm});
            skLineSegment(sketch, "E621", {"start": v(34.99, -17.6) * mm, "end": v(34.83, -17.62) * mm});
            skLineSegment(sketch, "E622", {"start": v(34.83, -17.62) * mm, "end": v(34.68, -17.63) * mm});
            skLineSegment(sketch, "E623", {"start": v(34.68, -17.63) * mm, "end": v(-34.67, -17.63) * mm});
            skLineSegment(sketch, "E624", {"start": v(-34.67, -17.63) * mm, "end": v(-34.83, -17.62) * mm});
            skLineSegment(sketch, "E625", {"start": v(-34.83, -17.62) * mm, "end": v(-34.99, -17.6) * mm});
            skLineSegment(sketch, "E626", {"start": v(-34.99, -17.6) * mm, "end": v(-35.14, -17.57) * mm});
            skLineSegment(sketch, "E627", {"start": v(-35.14, -17.57) * mm, "end": v(-35.3, -17.53) * mm});
            skLineSegment(sketch, "E628", {"start": v(-35.3, -17.53) * mm, "end": v(-35.44, -17.47) * mm});
            skLineSegment(sketch, "E629", {"start": v(-35.44, -17.47) * mm, "end": v(-35.58, -17.4) * mm});
            skLineSegment(sketch, "E630", {"start": v(-35.58, -17.4) * mm, "end": v(-35.72, -17.33) * mm});
            skLineSegment(sketch, "E631", {"start": v(-35.72, -17.33) * mm, "end": v(-35.85, -17.24) * mm});
            skLineSegment(sketch, "E632", {"start": v(-35.85, -17.24) * mm, "end": v(-35.97, -17.15) * mm});
            skLineSegment(sketch, "E633", {"start": v(-35.97, -17.15) * mm, "end": v(-36.1, -17.04) * mm});
            skLineSegment(sketch, "E634", {"start": v(-36.1, -17.04) * mm, "end": v(-36.2, -16.92) * mm});
            skLineSegment(sketch, "E635", {"start": v(-36.2, -16.92) * mm, "end": v(-36.3, -16.8) * mm});
            skLineSegment(sketch, "E636", {"start": v(-36.3, -16.8) * mm, "end": v(-36.38, -16.67) * mm});
            skLineSegment(sketch, "E637", {"start": v(-36.38, -16.67) * mm, "end": v(-36.46, -16.53) * mm});
            skLineSegment(sketch, "E638", {"start": v(-36.46, -16.53) * mm, "end": v(-36.52, -16.4) * mm});
            skLineSegment(sketch, "E639", {"start": v(-36.52, -16.4) * mm, "end": v(-36.58, -16.24) * mm});
            skLineSegment(sketch, "E640", {"start": v(-36.58, -16.24) * mm, "end": v(-36.62, -16.1) * mm});
            skLineSegment(sketch, "E641", {"start": v(-36.62, -16.1) * mm, "end": v(-36.65, -15.94) * mm});
            skLineSegment(sketch, "E642", {"start": v(-36.65, -15.94) * mm, "end": v(-36.67, -15.78) * mm});
            skLineSegment(sketch, "E643", {"start": v(-36.67, -15.78) * mm, "end": v(-36.68, -15.62) * mm});
            skLineSegment(sketch, "E644", {"start": v(-36.68, -15.62) * mm, "end": v(-36.67, 15.62) * mm});
            skLineSegment(sketch, "E645", {"start": v(-36.67, 15.62) * mm, "end": v(-36.67, 15.78) * mm});
            skLineSegment(sketch, "E646", {"start": v(-36.67, 15.78) * mm, "end": v(-36.65, 15.94) * mm});
            skLineSegment(sketch, "E647", {"start": v(-36.65, 15.94) * mm, "end": v(-36.62, 16.1) * mm});
            skLineSegment(sketch, "E648", {"start": v(-36.62, 16.1) * mm, "end": v(-36.58, 16.24) * mm});
            skLineSegment(sketch, "E649", {"start": v(-36.58, 16.24) * mm, "end": v(-36.52, 16.4) * mm});
            skLineSegment(sketch, "E650", {"start": v(-36.52, 16.4) * mm, "end": v(-36.46, 16.53) * mm});
            skLineSegment(sketch, "E651", {"start": v(-36.46, 16.53) * mm, "end": v(-36.38, 16.67) * mm});
            skLineSegment(sketch, "E652", {"start": v(-36.38, 16.67) * mm, "end": v(-36.3, 16.8) * mm});
            skLineSegment(sketch, "E653", {"start": v(-36.3, 16.8) * mm, "end": v(-36.2, 16.92) * mm});
            skLineSegment(sketch, "E654", {"start": v(-36.2, 16.92) * mm, "end": v(-36.1, 17.04) * mm});
            skLineSegment(sketch, "E655", {"start": v(-36.1, 17.04) * mm, "end": v(-35.97, 17.15) * mm});
            skLineSegment(sketch, "E656", {"start": v(-35.97, 17.15) * mm, "end": v(-35.85, 17.24) * mm});
            skLineSegment(sketch, "E657", {"start": v(-35.85, 17.24) * mm, "end": v(-35.72, 17.33) * mm});
            skLineSegment(sketch, "E658", {"start": v(-35.72, 17.33) * mm, "end": v(-35.58, 17.4) * mm});
            skLineSegment(sketch, "E659", {"start": v(-35.58, 17.4) * mm, "end": v(-35.44, 17.47) * mm});
            skLineSegment(sketch, "E660", {"start": v(-35.44, 17.47) * mm, "end": v(-35.3, 17.53) * mm});
            skLineSegment(sketch, "E661", {"start": v(-35.3, 17.53) * mm, "end": v(-35.14, 17.57) * mm});
            skLineSegment(sketch, "E662", {"start": v(-35.14, 17.57) * mm, "end": v(-34.99, 17.6) * mm});
            skLineSegment(sketch, "E663", {"start": v(-34.99, 17.6) * mm, "end": v(-34.83, 17.62) * mm});
            skLineSegment(sketch, "E664", {"start": v(-34.83, 17.62) * mm, "end": v(-34.67, 17.63) * mm});
            skLineSegment(sketch, "E665", {"start": v(-34.67, 17.63) * mm, "end": v(34.68, 17.62) * mm});
            skLineSegment(sketch, "E666", {"start": v(33.14, -13.2) * mm, "end": v(32.75, -13.4) * mm});
            skLineSegment(sketch, "E667", {"start": v(32.75, -13.4) * mm, "end": v(32.44, -13.7) * mm});
            skLineSegment(sketch, "E668", {"start": v(32.44, -13.7) * mm, "end": v(32.24, -14.1) * mm});
            skLineSegment(sketch, "E669", {"start": v(32.24, -14.1) * mm, "end": v(32.18, -14.53) * mm});
            skLineSegment(sketch, "E670", {"start": v(32.18, -14.53) * mm, "end": v(32.24, -14.96) * mm});
            skLineSegment(sketch, "E671", {"start": v(32.24, -14.96) * mm, "end": v(32.44, -15.35) * mm});
            skLineSegment(sketch, "E672", {"start": v(32.44, -15.35) * mm, "end": v(32.75, -15.66) * mm});
            skLineSegment(sketch, "E673", {"start": v(32.75, -15.66) * mm, "end": v(33.14, -15.86) * mm});
            skLineSegment(sketch, "E674", {"start": v(33.14, -15.86) * mm, "end": v(33.58, -15.93) * mm});
            skLineSegment(sketch, "E675", {"start": v(33.58, -15.93) * mm, "end": v(34, -15.86) * mm});
            skLineSegment(sketch, "E676", {"start": v(34, -15.86) * mm, "end": v(34.4, -15.66) * mm});
            skLineSegment(sketch, "E677", {"start": v(34.4, -15.66) * mm, "end": v(34.7, -15.35) * mm});
            skLineSegment(sketch, "E678", {"start": v(34.7, -15.35) * mm, "end": v(34.9, -14.96) * mm});
            skLineSegment(sketch, "E679", {"start": v(34.9, -14.96) * mm, "end": v(34.98, -14.53) * mm});
            skLineSegment(sketch, "E680", {"start": v(34.98, -14.53) * mm, "end": v(34.9, -14.1) * mm});
            skLineSegment(sketch, "E681", {"start": v(34.9, -14.1) * mm, "end": v(34.7, -13.7) * mm});
            skLineSegment(sketch, "E682", {"start": v(34.7, -13.7) * mm, "end": v(34.4, -13.4) * mm});
            skLineSegment(sketch, "E683", {"start": v(34.4, -13.4) * mm, "end": v(34, -13.2) * mm});
            skLineSegment(sketch, "E684", {"start": v(34, -13.2) * mm, "end": v(33.58, -13.13) * mm});
            skLineSegment(sketch, "E685", {"start": v(33.58, -13.13) * mm, "end": v(33.14, -13.2) * mm});
            skLineSegment(sketch, "E686", {"start": v(-34, -13.2) * mm, "end": v(-34.4, -13.4) * mm});
            skLineSegment(sketch, "E687", {"start": v(-34.4, -13.4) * mm, "end": v(-34.7, -13.7) * mm});
            skLineSegment(sketch, "E688", {"start": v(-34.7, -13.7) * mm, "end": v(-34.9, -14.1) * mm});
            skLineSegment(sketch, "E689", {"start": v(-34.9, -14.1) * mm, "end": v(-34.98, -14.53) * mm});
            skLineSegment(sketch, "E690", {"start": v(-34.98, -14.53) * mm, "end": v(-34.9, -14.96) * mm});
            skLineSegment(sketch, "E691", {"start": v(-34.9, -14.96) * mm, "end": v(-34.7, -15.35) * mm});
            skLineSegment(sketch, "E692", {"start": v(-34.7, -15.35) * mm, "end": v(-34.4, -15.66) * mm});
            skLineSegment(sketch, "E693", {"start": v(-34.4, -15.66) * mm, "end": v(-34, -15.86) * mm});
            skLineSegment(sketch, "E694", {"start": v(-34, -15.86) * mm, "end": v(-33.58, -15.93) * mm});
            skLineSegment(sketch, "E695", {"start": v(-33.58, -15.93) * mm, "end": v(-33.14, -15.86) * mm});
            skLineSegment(sketch, "E696", {"start": v(-33.14, -15.86) * mm, "end": v(-32.75, -15.66) * mm});
            skLineSegment(sketch, "E697", {"start": v(-32.75, -15.66) * mm, "end": v(-32.44, -15.35) * mm});
            skLineSegment(sketch, "E698", {"start": v(-32.44, -15.35) * mm, "end": v(-32.24, -14.96) * mm});
            skLineSegment(sketch, "E699", {"start": v(-32.24, -14.96) * mm, "end": v(-32.18, -14.53) * mm});
            skLineSegment(sketch, "E700", {"start": v(-32.18, -14.53) * mm, "end": v(-32.24, -14.1) * mm});
            skLineSegment(sketch, "E701", {"start": v(-32.24, -14.1) * mm, "end": v(-32.44, -13.7) * mm});
            skLineSegment(sketch, "E702", {"start": v(-32.44, -13.7) * mm, "end": v(-32.75, -13.4) * mm});
            skLineSegment(sketch, "E703", {"start": v(-32.75, -13.4) * mm, "end": v(-33.14, -13.2) * mm});
            skLineSegment(sketch, "E704", {"start": v(-33.14, -13.2) * mm, "end": v(-33.58, -13.13) * mm});
            skLineSegment(sketch, "E705", {"start": v(-33.58, -13.13) * mm, "end": v(-34, -13.2) * mm});
            skLineSegment(sketch, "E706", {"start": v(-28.58, 9.53) * mm, "end": v(28.58, 9.53) * mm});
            skLineSegment(sketch, "E707", {"start": v(28.58, 9.53) * mm, "end": v(28.58, -9.53) * mm});
            skLineSegment(sketch, "E708", {"start": v(28.58, -9.53) * mm, "end": v(-28.58, -9.53) * mm});
            skLineSegment(sketch, "E709", {"start": v(-28.58, -9.53) * mm, "end": v(-28.58, 9.53) * mm});
            skLineSegment(sketch, "E710", {"start": v(33.14, 15.86) * mm, "end": v(32.75, 15.66) * mm});
            skLineSegment(sketch, "E711", {"start": v(32.75, 15.66) * mm, "end": v(32.44, 15.35) * mm});
            skLineSegment(sketch, "E712", {"start": v(32.44, 15.35) * mm, "end": v(32.24, 14.96) * mm});
            skLineSegment(sketch, "E713", {"start": v(32.24, 14.96) * mm, "end": v(32.18, 14.53) * mm});
            skLineSegment(sketch, "E714", {"start": v(32.18, 14.53) * mm, "end": v(32.24, 14.1) * mm});
            skLineSegment(sketch, "E715", {"start": v(32.24, 14.1) * mm, "end": v(32.44, 13.7) * mm});
            skLineSegment(sketch, "E716", {"start": v(32.44, 13.7) * mm, "end": v(32.75, 13.4) * mm});
            skLineSegment(sketch, "E717", {"start": v(32.75, 13.4) * mm, "end": v(33.14, 13.2) * mm});
            skLineSegment(sketch, "E718", {"start": v(33.14, 13.2) * mm, "end": v(33.58, 13.13) * mm});
            skLineSegment(sketch, "E719", {"start": v(33.58, 13.13) * mm, "end": v(34, 13.2) * mm});
            skLineSegment(sketch, "E720", {"start": v(34, 13.2) * mm, "end": v(34.4, 13.4) * mm});
            skLineSegment(sketch, "E721", {"start": v(34.4, 13.4) * mm, "end": v(34.7, 13.7) * mm});
            skLineSegment(sketch, "E722", {"start": v(34.7, 13.7) * mm, "end": v(34.9, 14.1) * mm});
            skLineSegment(sketch, "E723", {"start": v(34.9, 14.1) * mm, "end": v(34.98, 14.53) * mm});
            skLineSegment(sketch, "E724", {"start": v(34.98, 14.53) * mm, "end": v(34.9, 14.96) * mm});
            skLineSegment(sketch, "E725", {"start": v(34.9, 14.96) * mm, "end": v(34.7, 15.35) * mm});
            skLineSegment(sketch, "E726", {"start": v(34.7, 15.35) * mm, "end": v(34.4, 15.66) * mm});
            skLineSegment(sketch, "E727", {"start": v(34.4, 15.66) * mm, "end": v(34, 15.86) * mm});
            skLineSegment(sketch, "E728", {"start": v(34, 15.86) * mm, "end": v(33.58, 15.93) * mm});
            skLineSegment(sketch, "E729", {"start": v(33.58, 15.93) * mm, "end": v(33.14, 15.86) * mm});
            skLineSegment(sketch, "E730", {"start": v(-34, 15.86) * mm, "end": v(-34.4, 15.66) * mm});
            skLineSegment(sketch, "E731", {"start": v(-34.4, 15.66) * mm, "end": v(-34.7, 15.35) * mm});
            skLineSegment(sketch, "E732", {"start": v(-34.7, 15.35) * mm, "end": v(-34.9, 14.96) * mm});
            skLineSegment(sketch, "E733", {"start": v(-34.9, 14.96) * mm, "end": v(-34.98, 14.53) * mm});
            skLineSegment(sketch, "E734", {"start": v(-34.98, 14.53) * mm, "end": v(-34.9, 14.1) * mm});
            skLineSegment(sketch, "E735", {"start": v(-34.9, 14.1) * mm, "end": v(-34.7, 13.7) * mm});
            skLineSegment(sketch, "E736", {"start": v(-34.7, 13.7) * mm, "end": v(-34.4, 13.4) * mm});
            skLineSegment(sketch, "E737", {"start": v(-34.4, 13.4) * mm, "end": v(-34, 13.2) * mm});
            skLineSegment(sketch, "E738", {"start": v(-34, 13.2) * mm, "end": v(-33.58, 13.13) * mm});
            skLineSegment(sketch, "E739", {"start": v(-33.58, 13.13) * mm, "end": v(-33.14, 13.2) * mm});
            skLineSegment(sketch, "E740", {"start": v(-33.14, 13.2) * mm, "end": v(-32.75, 13.4) * mm});
            skLineSegment(sketch, "E741", {"start": v(-32.75, 13.4) * mm, "end": v(-32.44, 13.7) * mm});
            skLineSegment(sketch, "E742", {"start": v(-32.44, 13.7) * mm, "end": v(-32.24, 14.1) * mm});
            skLineSegment(sketch, "E743", {"start": v(-32.24, 14.1) * mm, "end": v(-32.18, 14.53) * mm});
            skLineSegment(sketch, "E744", {"start": v(-32.18, 14.53) * mm, "end": v(-32.24, 14.96) * mm});
            skLineSegment(sketch, "E745", {"start": v(-32.24, 14.96) * mm, "end": v(-32.44, 15.35) * mm});
            skLineSegment(sketch, "E746", {"start": v(-32.44, 15.35) * mm, "end": v(-32.75, 15.66) * mm});
            skLineSegment(sketch, "E747", {"start": v(-32.75, 15.66) * mm, "end": v(-33.14, 15.86) * mm});
            skLineSegment(sketch, "E748", {"start": v(-33.14, 15.86) * mm, "end": v(-33.58, 15.93) * mm});
            skLineSegment(sketch, "E749", {"start": v(-33.58, 15.93) * mm, "end": v(-34, 15.86) * mm});
            skSolve(sketch);
        }
        {
            var Q0;
            Q0 = qSketchRegion(id + "F9", true);
            extrude(context, id + "F10", {"entities" : qUnion([Q0]), "depth" : (getVariable(context, 'Thickness') * 2) * mm, "offsetDistance" : 25 * mm});
        }
    });
